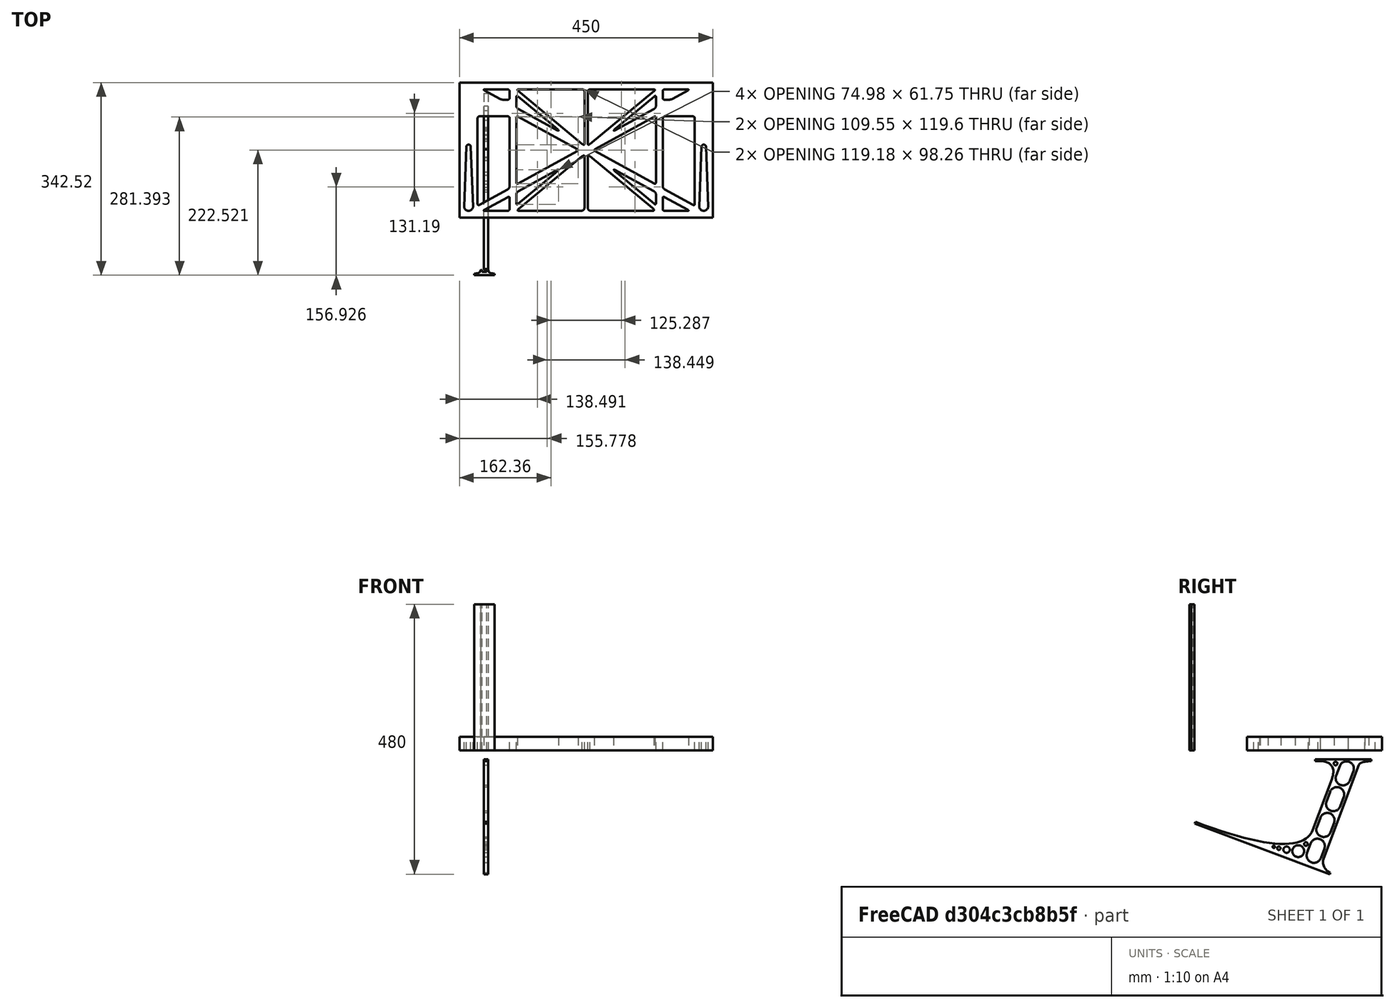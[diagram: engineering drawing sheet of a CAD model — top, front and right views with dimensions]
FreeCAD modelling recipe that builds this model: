
FCSTD DOCUMENT  (FreeCAD 0.19R0.19.2)
Label: laptopStand162FCStd
License: All rights reserved
LicenseURL: http://en.wikipedia.org/wiki/All_rights_reserved
objects: Sketcher::SketchObject×4, Part::Extrusion×3
note: 7 computed .brp shape members not serialized (recipe doc carries the construction recipe); baked Part::Feature solids carry a one-line shape summary decoded from their .brp

FEATURE [Sketcher::SketchObject] Sketch
  FullyConstrained = false
  sketch-geometry (349):
    g0: LineSegment StartX=-10.9272 StartY=-82.7794 StartZ=0 EndX=46.0728 EndY=-51.4823 EndZ=0
    g1: LineSegment StartX=-10.9272 StartY=76.4095 StartZ=0 EndX=-10.9272 EndY=-82.7794 EndZ=0
    g2: LineSegment StartX=46.0728 StartY=76.4095 StartZ=0 EndX=46.0728 EndY=-51.4823 EndZ=0
    g3: LineSegment StartX=-42.9272 StartY=136.221 StartZ=0 EndX=-42.9272 EndY=-103.779 EndZ=0
    g4: LineSegment StartX=407.073 StartY=136.221 StartZ=0 EndX=407.073 EndY=-103.779 EndZ=0
    g5: ArcOfCircle CenterX=-26.9272 CenterY=-83.7794 CenterZ=0 NormalX=0 NormalY=0 NormalZ=1 AngleXU=0 Radius=8 StartAngle=3.14159 EndAngle=6.28319
    g6: ArcOfCircle CenterX=391.073 CenterY=22.1087 CenterZ=0 NormalX=0 NormalY=0 NormalZ=1 AngleXU=0 Radius=8 StartAngle=-4.4e-15 EndAngle=3.14159
    g7: LineSegment StartX=399.073 StartY=22.1087 StartZ=0 EndX=399.073 EndY=-83.7794 EndZ=0
    g8: LineSegment StartX=383.073 StartY=22.1087 StartZ=0 EndX=383.073 EndY=-83.7794 EndZ=0
    g9: ArcOfCircle CenterX=391.073 CenterY=-83.7794 CenterZ=0 NormalX=0 NormalY=0 NormalZ=1 AngleXU=0 Radius=8 StartAngle=3.14159 EndAngle=6.28319
    g10: Circle CenterX=175.022 CenterY=27.0628 CenterZ=0 NormalX=0 NormalY=0 NormalZ=1 AngleXU=0 Radius=1
    g11: Circle CenterX=179.022 CenterY=24.8665 CenterZ=0 NormalX=0 NormalY=0 NormalZ=1 AngleXU=0 Radius=1
    g12: Circle CenterX=179.022 CenterY=27.0628 CenterZ=0 NormalX=0 NormalY=0 NormalZ=1 AngleXU=0 Radius=1
    g13: BSplineCurve PolesCount=3 KnotsCount=2 Degree=2 IsPeriodic=0
    g14: GeomPoint X=175.022 Y=27.0628 Z=0
    g15: GeomPoint X=179.022 Y=27.0628 Z=0
    g16: Circle CenterX=189.124 CenterY=27.0628 CenterZ=0 NormalX=0 NormalY=0 NormalZ=1 AngleXU=0 Radius=1
    g17: Circle CenterX=185.124 CenterY=24.8665 CenterZ=0 NormalX=0 NormalY=0 NormalZ=1 AngleXU=0 Radius=1
    g18: Circle CenterX=185.124 CenterY=27.0628 CenterZ=0 NormalX=0 NormalY=0 NormalZ=1 AngleXU=0 Radius=1
    g19: BSplineCurve PolesCount=3 KnotsCount=2 Degree=2 IsPeriodic=0
    g20: GeomPoint X=189.124 Y=27.0628 Z=0
    g21: GeomPoint X=185.124 Y=27.0628 Z=0
    g22: Circle CenterX=175.022 CenterY=5.37834 CenterZ=0 NormalX=0 NormalY=0 NormalZ=1 AngleXU=0 Radius=1
    g23: Circle CenterX=179.022 CenterY=7.57463 CenterZ=0 NormalX=0 NormalY=0 NormalZ=1 AngleXU=0 Radius=1
    g24: Circle CenterX=179.022 CenterY=5.34704 CenterZ=0 NormalX=0 NormalY=0 NormalZ=1 AngleXU=0 Radius=1
    g25: BSplineCurve PolesCount=3 KnotsCount=2 Degree=2 IsPeriodic=0
    g26: GeomPoint X=175.022 Y=5.37834 Z=0
    g27: GeomPoint X=179.022 Y=5.34704 Z=0
    g28: Circle CenterX=189.124 CenterY=5.37834 CenterZ=0 NormalX=0 NormalY=0 NormalZ=1 AngleXU=0 Radius=1
    g29: Circle CenterX=185.124 CenterY=7.57463 CenterZ=0 NormalX=0 NormalY=0 NormalZ=1 AngleXU=0 Radius=1
    g30: Circle CenterX=185.124 CenterY=5.34704 CenterZ=0 NormalX=0 NormalY=0 NormalZ=1 AngleXU=0 Radius=1
    g31: BSplineCurve PolesCount=3 KnotsCount=2 Degree=2 IsPeriodic=0
    g32: GeomPoint X=189.124 Y=5.37834 Z=0
    g33: GeomPoint X=185.124 Y=5.34704 Z=0
    g34: Circle CenterX=165.871 CenterY=18.1458 CenterZ=0 NormalX=0 NormalY=0 NormalZ=1 AngleXU=0 Radius=1
    g35: Circle CenterX=169.377 CenterY=16.2206 CenterZ=0 NormalX=0 NormalY=0 NormalZ=1 AngleXU=0 Radius=1
    g36: Circle CenterX=165.871 CenterY=14.2954 CenterZ=0 NormalX=0 NormalY=0 NormalZ=1 AngleXU=0 Radius=1
    g37: BSplineCurve PolesCount=3 KnotsCount=2 Degree=2 IsPeriodic=0
    g38: GeomPoint X=165.871 Y=18.1458 Z=0
    g39: GeomPoint X=165.871 Y=14.2954 Z=0
    g40: Circle CenterX=198.275 CenterY=18.1458 CenterZ=0 NormalX=0 NormalY=0 NormalZ=1 AngleXU=0 Radius=1
    g41: Circle CenterX=194.768 CenterY=16.2206 CenterZ=0 NormalX=0 NormalY=0 NormalZ=1 AngleXU=0 Radius=1
    g42: Circle CenterX=198.275 CenterY=14.2954 CenterZ=0 NormalX=0 NormalY=0 NormalZ=1 AngleXU=0 Radius=1
    g43: BSplineCurve PolesCount=3 KnotsCount=2 Degree=2 IsPeriodic=0
    g44: GeomPoint X=198.275 Y=18.1458 Z=0
    g45: GeomPoint X=198.275 Y=14.2954 Z=0
    g46: LineSegment StartX=407.073 StartY=-103.779 StartZ=0 EndX=-42.9272 EndY=-103.779 EndZ=0
    g47: LineSegment StartX=407.073 StartY=136.221 StartZ=0 EndX=-42.9272 EndY=136.221 EndZ=0
    g48: LineSegment StartX=46.0728 StartY=76.4095 StartZ=0 EndX=-10.9272 EndY=76.4095 EndZ=0
    g49: Circle CenterX=125.607 CenterY=54.1951 CenterZ=0 NormalX=0 NormalY=0 NormalZ=1 AngleXU=0 Radius=1
    g50: Circle CenterX=139.632 CenterY=46.4944 CenterZ=0 NormalX=0 NormalY=0 NormalZ=1 AngleXU=0 Radius=1
    g51: Circle CenterX=127.326 CenterY=56.7187 CenterZ=0 NormalX=0 NormalY=0 NormalZ=1 AngleXU=0 Radius=1
    g52: BSplineCurve PolesCount=3 KnotsCount=2 Degree=2 IsPeriodic=0
    g53: GeomPoint X=125.607 Y=54.1951 Z=0
    g54: GeomPoint X=127.326 Y=56.7187 Z=0
    g55: Circle CenterX=236.821 CenterY=56.7187 CenterZ=0 NormalX=0 NormalY=0 NormalZ=1 AngleXU=0 Radius=1
    g56: Circle CenterX=224.513 CenterY=46.4944 CenterZ=0 NormalX=0 NormalY=0 NormalZ=1 AngleXU=0 Radius=1
    g57: Circle CenterX=238.538 CenterY=54.1951 CenterZ=0 NormalX=0 NormalY=0 NormalZ=1 AngleXU=0 Radius=1
    g58: BSplineCurve PolesCount=3 KnotsCount=2 Degree=2 IsPeriodic=0
    g59: GeomPoint X=236.821 Y=56.7187 Z=0
    g60: GeomPoint X=238.538 Y=54.1951 Z=0
    g61: Circle CenterX=238.538 CenterY=-21.7539 CenterZ=0 NormalX=0 NormalY=0 NormalZ=1 AngleXU=0 Radius=1
    g62: Circle CenterX=224.513 CenterY=-14.0532 CenterZ=0 NormalX=0 NormalY=0 NormalZ=1 AngleXU=0 Radius=1
    g63: Circle CenterX=236.821 CenterY=-24.2775 CenterZ=0 NormalX=0 NormalY=0 NormalZ=1 AngleXU=0 Radius=1
    g64: BSplineCurve PolesCount=3 KnotsCount=2 Degree=2 IsPeriodic=0
    g65: GeomPoint X=238.538 Y=-21.7539 Z=0
    g66: GeomPoint X=236.821 Y=-24.2775 Z=0
    g67: Circle CenterX=125.607 CenterY=-21.7539 CenterZ=0 NormalX=0 NormalY=0 NormalZ=1 AngleXU=0 Radius=1
    g68: Circle CenterX=139.632 CenterY=-14.0532 CenterZ=0 NormalX=0 NormalY=0 NormalZ=1 AngleXU=0 Radius=1
    g69: Circle CenterX=127.325 CenterY=-24.2775 CenterZ=0 NormalX=0 NormalY=0 NormalZ=1 AngleXU=0 Radius=1
    g70: BSplineCurve PolesCount=3 KnotsCount=2 Degree=2 IsPeriodic=0
    g71: GeomPoint X=125.607 Y=-21.7539 Z=0
    g72: GeomPoint X=127.325 Y=-24.2775 Z=0
    g73: Circle CenterX=302.996 CenterY=111.695 CenterZ=0 NormalX=0 NormalY=0 NormalZ=1 AngleXU=0 Radius=1
    g74: Circle CenterX=306.073 CenterY=114.251 CenterZ=0 NormalX=0 NormalY=0 NormalZ=1 AngleXU=0 Radius=1
    g75: Circle CenterX=306.073 CenterY=110.251 CenterZ=0 NormalX=0 NormalY=0 NormalZ=1 AngleXU=0 Radius=1
    g76: BSplineCurve PolesCount=3 KnotsCount=2 Degree=2 IsPeriodic=0
    g77: GeomPoint X=302.996 Y=111.695 Z=0
    g78: GeomPoint X=306.073 Y=110.251 Z=0
    g79: Circle CenterX=306.073 CenterY=95.2763 CenterZ=0 NormalX=0 NormalY=0 NormalZ=1 AngleXU=0 Radius=1
    g80: Circle CenterX=306.073 CenterY=91.2763 CenterZ=0 NormalX=0 NormalY=0 NormalZ=1 AngleXU=0 Radius=1
    g81: Circle CenterX=302.567 CenterY=89.3511 CenterZ=0 NormalX=0 NormalY=0 NormalZ=1 AngleXU=0 Radius=1
    g82: BSplineCurve PolesCount=3 KnotsCount=2 Degree=2 IsPeriodic=0
    g83: GeomPoint X=306.073 Y=95.2763 Z=0
    g84: GeomPoint X=302.567 Y=89.3511 Z=0
    g85: LineSegment StartX=306.073 StartY=110.251 StartZ=0 EndX=306.073 EndY=95.2763 EndZ=0
    g86: LineSegment StartX=302.996 StartY=111.695 StartZ=0 EndX=236.821 EndY=56.7187 EndZ=0
    g87: LineSegment StartX=238.538 StartY=54.1951 StartZ=0 EndX=302.567 EndY=89.3511 EndZ=0
    g88: Circle CenterX=61.1496 CenterY=111.695 CenterZ=0 NormalX=0 NormalY=0 NormalZ=1 AngleXU=0 Radius=1
    g89: Circle CenterX=58.0728 CenterY=114.251 CenterZ=0 NormalX=0 NormalY=0 NormalZ=1 AngleXU=0 Radius=1
    g90: Circle CenterX=58.0728 CenterY=110.251 CenterZ=0 NormalX=0 NormalY=0 NormalZ=1 AngleXU=0 Radius=1
    g91: BSplineCurve PolesCount=3 KnotsCount=2 Degree=2 IsPeriodic=0
    g92: GeomPoint X=61.1496 Y=111.695 Z=0
    g93: GeomPoint X=58.0728 Y=110.251 Z=0
    g94: Circle CenterX=61.5791 CenterY=89.3511 CenterZ=0 NormalX=0 NormalY=0 NormalZ=1 AngleXU=0 Radius=1
    g95: Circle CenterX=58.0728 CenterY=91.2763 CenterZ=0 NormalX=0 NormalY=0 NormalZ=1 AngleXU=0 Radius=1
    g96: Circle CenterX=58.0728 CenterY=95.2763 CenterZ=0 NormalX=0 NormalY=0 NormalZ=1 AngleXU=0 Radius=1
    g97: BSplineCurve PolesCount=3 KnotsCount=2 Degree=2 IsPeriodic=0
    g98: GeomPoint X=61.5791 Y=89.3511 Z=0
    g99: GeomPoint X=58.0728 Y=95.2763 Z=0
    g100: LineSegment StartX=58.0728 StartY=110.251 StartZ=0 EndX=58.0728 EndY=95.2763 EndZ=0
    g101: LineSegment StartX=61.1496 StartY=111.695 StartZ=0 EndX=127.326 EndY=56.7187 EndZ=0
    g102: LineSegment StartX=125.607 StartY=54.1951 StartZ=0 EndX=61.5791 EndY=89.3511 EndZ=0
    g103: Circle CenterX=61.5791 CenterY=-56.9099 CenterZ=0 NormalX=0 NormalY=0 NormalZ=1 AngleXU=0 Radius=1
    g104: Circle CenterX=58.0728 CenterY=-58.8351 CenterZ=0 NormalX=0 NormalY=0 NormalZ=1 AngleXU=0 Radius=1
    g105: Circle CenterX=58.0728 CenterY=-62.8351 CenterZ=0 NormalX=0 NormalY=0 NormalZ=1 AngleXU=0 Radius=1
    g106: BSplineCurve PolesCount=3 KnotsCount=2 Degree=2 IsPeriodic=0
    g107: GeomPoint X=61.5791 Y=-56.9099 Z=0
    g108: GeomPoint X=58.0728 Y=-62.8351 Z=0
    g109: Circle CenterX=58.0728 CenterY=-77.8102 CenterZ=0 NormalX=0 NormalY=0 NormalZ=1 AngleXU=0 Radius=1
    g110: Circle CenterX=58.0728 CenterY=-81.8102 CenterZ=0 NormalX=0 NormalY=0 NormalZ=1 AngleXU=0 Radius=1
    g111: Circle CenterX=61.1496 CenterY=-79.2541 CenterZ=0 NormalX=0 NormalY=0 NormalZ=1 AngleXU=0 Radius=1
    g112: BSplineCurve PolesCount=3 KnotsCount=2 Degree=2 IsPeriodic=0
    g113: GeomPoint X=58.0728 Y=-77.8102 Z=0
    g114: GeomPoint X=61.1496 Y=-79.2541 Z=0
    g115: LineSegment StartX=58.0728 StartY=-62.8351 StartZ=0 EndX=58.0728 EndY=-77.8102 EndZ=0
    g116: LineSegment StartX=61.1496 StartY=-79.2541 StartZ=0 EndX=127.325 EndY=-24.2775 EndZ=0
    g117: LineSegment StartX=125.607 StartY=-21.7539 StartZ=0 EndX=61.5791 EndY=-56.9099 EndZ=0
    g118: Circle CenterX=302.567 CenterY=-56.9099 CenterZ=0 NormalX=0 NormalY=0 NormalZ=1 AngleXU=0 Radius=1
    g119: Circle CenterX=306.073 CenterY=-58.8351 CenterZ=0 NormalX=0 NormalY=0 NormalZ=1 AngleXU=0 Radius=1
    g120: Circle CenterX=306.073 CenterY=-62.8351 CenterZ=0 NormalX=0 NormalY=0 NormalZ=1 AngleXU=0 Radius=1
    g121: BSplineCurve PolesCount=3 KnotsCount=2 Degree=2 IsPeriodic=0
    g122: GeomPoint X=302.567 Y=-56.9099 Z=0
    g123: GeomPoint X=306.073 Y=-62.8351 Z=0
    g124: Circle CenterX=302.996 CenterY=-79.2541 CenterZ=0 NormalX=0 NormalY=0 NormalZ=1 AngleXU=0 Radius=1
    g125: Circle CenterX=306.073 CenterY=-81.8102 CenterZ=0 NormalX=0 NormalY=0 NormalZ=1 AngleXU=0 Radius=1
    g126: Circle CenterX=306.073 CenterY=-77.8102 CenterZ=0 NormalX=0 NormalY=0 NormalZ=1 AngleXU=0 Radius=1
    g127: BSplineCurve PolesCount=3 KnotsCount=2 Degree=2 IsPeriodic=0
    g128: GeomPoint X=302.996 Y=-79.2541 Z=0
    g129: GeomPoint X=306.073 Y=-77.8102 Z=0
    g130: LineSegment StartX=306.073 StartY=-62.8351 StartZ=0 EndX=306.073 EndY=-77.8102 EndZ=0
    g131: LineSegment StartX=302.996 StartY=-79.2541 StartZ=0 EndX=236.821 EndY=-24.2775 EndZ=0
    g132: LineSegment StartX=238.538 StartY=-21.7539 StartZ=0 EndX=302.567 EndY=-56.9099 EndZ=0
    g133: Circle CenterX=61.6457 CenterY=-88.8112 CenterZ=0 NormalX=0 NormalY=0 NormalZ=1 AngleXU=0 Radius=1
    g134: Circle CenterX=58.0728 CenterY=-91.7794 CenterZ=0 NormalX=0 NormalY=0 NormalZ=1 AngleXU=0 Radius=1
    g135: Circle CenterX=63.9135 CenterY=-91.7794 CenterZ=0 NormalX=0 NormalY=0 NormalZ=1 AngleXU=0 Radius=1
    g136: BSplineCurve PolesCount=3 KnotsCount=2 Degree=2 IsPeriodic=0
    g137: GeomPoint X=61.6457 Y=-88.8112 Z=0
    g138: GeomPoint X=63.9135 Y=-91.7794 Z=0
    g139: Circle CenterX=179.022 CenterY=-85.8163 CenterZ=0 NormalX=0 NormalY=0 NormalZ=1 AngleXU=0 Radius=1
    g140: Circle CenterX=179.022 CenterY=-91.7794 CenterZ=0 NormalX=0 NormalY=0 NormalZ=1 AngleXU=0 Radius=1
    g141: Circle CenterX=171.895 CenterY=-91.7794 CenterZ=0 NormalX=0 NormalY=0 NormalZ=1 AngleXU=0 Radius=1
    g142: BSplineCurve PolesCount=3 KnotsCount=2 Degree=2 IsPeriodic=0
    g143: GeomPoint X=179.022 Y=-85.8163 Z=0
    g144: GeomPoint X=171.895 Y=-91.7794 Z=0
    g145: Circle CenterX=185.124 CenterY=-86.2028 CenterZ=0 NormalX=0 NormalY=0 NormalZ=1 AngleXU=0 Radius=1
    g146: Circle CenterX=185.124 CenterY=-91.7794 CenterZ=0 NormalX=0 NormalY=0 NormalZ=1 AngleXU=0 Radius=1
    g147: Circle CenterX=191.747 CenterY=-91.7794 CenterZ=0 NormalX=0 NormalY=0 NormalZ=1 AngleXU=0 Radius=1
    g148: BSplineCurve PolesCount=3 KnotsCount=2 Degree=2 IsPeriodic=0
    g149: GeomPoint X=185.124 Y=-86.2028 Z=0
    g150: GeomPoint X=191.747 Y=-91.7794 Z=0
    g151: Circle CenterX=299.888 CenterY=-86.6413 CenterZ=0 NormalX=0 NormalY=0 NormalZ=1 AngleXU=0 Radius=1
    g152: Circle CenterX=306.073 CenterY=-91.7794 CenterZ=0 NormalX=0 NormalY=0 NormalZ=1 AngleXU=0 Radius=1
    g153: Circle CenterX=298.776 CenterY=-91.7794 CenterZ=0 NormalX=0 NormalY=0 NormalZ=1 AngleXU=0 Radius=1
    g154: BSplineCurve PolesCount=3 KnotsCount=2 Degree=2 IsPeriodic=0
    g155: GeomPoint X=299.888 Y=-86.6413 Z=0
    g156: GeomPoint X=298.776 Y=-91.7794 Z=0
    g157: LineSegment StartX=189.124 StartY=5.37834 StartZ=0 EndX=299.888 EndY=-86.6413 EndZ=0
    g158: LineSegment StartX=298.776 StartY=-91.7794 StartZ=0 EndX=191.747 EndY=-91.7794 EndZ=0
    g159: LineSegment StartX=185.124 StartY=-86.2028 StartZ=0 EndX=185.124 EndY=5.34704 EndZ=0
    g160: LineSegment StartX=179.022 StartY=5.34704 StartZ=0 EndX=179.022 EndY=-85.8163 EndZ=0
    g161: LineSegment StartX=171.895 StartY=-91.7794 StartZ=0 EndX=63.9135 EndY=-91.7794 EndZ=0
    g162: LineSegment StartX=61.6457 StartY=-88.8112 StartZ=0 EndX=175.022 EndY=5.37834 EndZ=0
    g163: Circle CenterX=302.073 CenterY=124.221 CenterZ=0 NormalX=0 NormalY=0 NormalZ=1 AngleXU=0 Radius=1
    g164: Circle CenterX=306.073 CenterY=124.221 CenterZ=0 NormalX=0 NormalY=0 NormalZ=1 AngleXU=0 Radius=1
    g165: Circle CenterX=302.996 CenterY=121.665 CenterZ=0 NormalX=0 NormalY=0 NormalZ=1 AngleXU=0 Radius=1
    g166: BSplineCurve PolesCount=3 KnotsCount=2 Degree=2 IsPeriodic=0
    g167: GeomPoint X=302.073 Y=124.221 Z=0
    g168: GeomPoint X=302.996 Y=121.665 Z=0
    g169: Circle CenterX=189.124 CenterY=124.221 CenterZ=0 NormalX=0 NormalY=0 NormalZ=1 AngleXU=0 Radius=1
    g170: Circle CenterX=185.124 CenterY=124.221 CenterZ=0 NormalX=0 NormalY=0 NormalZ=1 AngleXU=0 Radius=1
    g171: Circle CenterX=185.124 CenterY=120.221 CenterZ=0 NormalX=0 NormalY=0 NormalZ=1 AngleXU=0 Radius=1
    g172: BSplineCurve PolesCount=3 KnotsCount=2 Degree=2 IsPeriodic=0
    g173: GeomPoint X=189.124 Y=124.221 Z=0
    g174: GeomPoint X=185.124 Y=120.221 Z=0
    g175: Circle CenterX=175.022 CenterY=124.221 CenterZ=0 NormalX=0 NormalY=0 NormalZ=1 AngleXU=0 Radius=1
    g176: Circle CenterX=179.022 CenterY=124.221 CenterZ=0 NormalX=0 NormalY=0 NormalZ=1 AngleXU=0 Radius=1
    g177: Circle CenterX=179.022 CenterY=120.221 CenterZ=0 NormalX=0 NormalY=0 NormalZ=1 AngleXU=0 Radius=1
    g178: BSplineCurve PolesCount=3 KnotsCount=2 Degree=2 IsPeriodic=0
    g179: GeomPoint X=175.022 Y=124.221 Z=0
    g180: GeomPoint X=179.022 Y=120.221 Z=0
    g181: Circle CenterX=62.0728 CenterY=124.221 CenterZ=0 NormalX=0 NormalY=0 NormalZ=1 AngleXU=0 Radius=1
    g182: Circle CenterX=58.0728 CenterY=124.221 CenterZ=0 NormalX=0 NormalY=0 NormalZ=1 AngleXU=0 Radius=1
    g183: Circle CenterX=61.1496 CenterY=121.665 CenterZ=0 NormalX=0 NormalY=0 NormalZ=1 AngleXU=0 Radius=1
    g184: BSplineCurve PolesCount=3 KnotsCount=2 Degree=2 IsPeriodic=0
    g185: GeomPoint X=62.0728 Y=124.221 Z=0
    g186: GeomPoint X=61.1496 Y=121.665 Z=0
    g187: LineSegment StartX=62.0728 StartY=124.221 StartZ=0 EndX=175.022 EndY=124.221 EndZ=0
    g188: LineSegment StartX=179.022 StartY=120.221 StartZ=0 EndX=179.022 EndY=27.0628 EndZ=0
    g189: LineSegment StartX=185.124 StartY=27.0628 StartZ=0 EndX=185.124 EndY=120.221 EndZ=0
    g190: LineSegment StartX=189.124 StartY=124.221 StartZ=0 EndX=302.073 EndY=124.221 EndZ=0
    g191: LineSegment StartX=302.996 StartY=121.665 StartZ=0 EndX=189.124 EndY=27.0628 EndZ=0
    g192: LineSegment StartX=175.022 StartY=27.0628 StartZ=0 EndX=61.1496 EndY=121.665 EndZ=0
    g193: Circle CenterX=61.5791 CenterY=75.4095 CenterZ=0 NormalX=0 NormalY=0 NormalZ=1 AngleXU=0 Radius=1
    g194: Circle CenterX=58.0728 CenterY=77.3346 CenterZ=0 NormalX=0 NormalY=0 NormalZ=1 AngleXU=0 Radius=1
    g195: Circle CenterX=58.0728 CenterY=73.3346 CenterZ=0 NormalX=0 NormalY=0 NormalZ=1 AngleXU=0 Radius=1
    g196: BSplineCurve PolesCount=3 KnotsCount=2 Degree=2 IsPeriodic=0
    g197: GeomPoint X=61.5791 Y=75.4095 Z=0
    g198: GeomPoint X=58.0728 Y=73.3346 Z=0
    g199: Circle CenterX=58.0728 CenterY=-40.8935 CenterZ=0 NormalX=0 NormalY=0 NormalZ=1 AngleXU=0 Radius=1
    g200: Circle CenterX=58.0728 CenterY=-44.8935 CenterZ=0 NormalX=0 NormalY=0 NormalZ=1 AngleXU=0 Radius=1
    g201: Circle CenterX=61.5791 CenterY=-42.9683 CenterZ=0 NormalX=0 NormalY=0 NormalZ=1 AngleXU=0 Radius=1
    g202: BSplineCurve PolesCount=3 KnotsCount=2 Degree=2 IsPeriodic=0
    g203: GeomPoint X=58.0728 Y=-40.8935 Z=0
    g204: GeomPoint X=61.5791 Y=-42.9683 Z=0
    g205: LineSegment StartX=61.5791 StartY=-42.9683 StartZ=0 EndX=165.871 EndY=14.2954 EndZ=0
    g206: LineSegment StartX=165.871 StartY=18.1458 StartZ=0 EndX=61.5791 EndY=75.4095 EndZ=0
    g207: LineSegment StartX=58.0728 StartY=73.3346 StartZ=0 EndX=58.0728 EndY=-40.8935 EndZ=0
    g208: Circle CenterX=302.567 CenterY=-42.9683 CenterZ=0 NormalX=0 NormalY=0 NormalZ=1 AngleXU=0 Radius=1
    g209: Circle CenterX=306.073 CenterY=-44.8935 CenterZ=0 NormalX=0 NormalY=0 NormalZ=1 AngleXU=0 Radius=1
    g210: Circle CenterX=306.073 CenterY=-40.8935 CenterZ=0 NormalX=0 NormalY=0 NormalZ=1 AngleXU=0 Radius=1
    g211: BSplineCurve PolesCount=3 KnotsCount=2 Degree=2 IsPeriodic=0
    g212: GeomPoint X=302.567 Y=-42.9683 Z=0
    g213: GeomPoint X=306.073 Y=-40.8935 Z=0
    g214: Circle CenterX=306.073 CenterY=73.3346 CenterZ=0 NormalX=0 NormalY=0 NormalZ=1 AngleXU=0 Radius=1
    g215: Circle CenterX=306.073 CenterY=77.3346 CenterZ=0 NormalX=0 NormalY=0 NormalZ=1 AngleXU=0 Radius=1
    g216: Circle CenterX=302.567 CenterY=75.4095 CenterZ=0 NormalX=0 NormalY=0 NormalZ=1 AngleXU=0 Radius=1
    g217: BSplineCurve PolesCount=3 KnotsCount=2 Degree=2 IsPeriodic=0
    g218: GeomPoint X=306.073 Y=73.3346 Z=0
    g219: GeomPoint X=302.567 Y=75.4095 Z=0
    g220: LineSegment StartX=302.567 StartY=-42.9683 StartZ=0 EndX=198.275 EndY=14.2954 EndZ=0
    g221: LineSegment StartX=198.275 StartY=18.1458 StartZ=0 EndX=302.567 EndY=75.4095 EndZ=0
    g222: LineSegment StartX=306.073 StartY=73.3346 StartZ=0 EndX=306.073 EndY=-40.8935 EndZ=0
    g223: LineSegment StartX=322.073 StartY=105.865 StartZ=0 EndX=328.643 EndY=105.865 EndZ=0
    g224: LineSegment StartX=318.073 StartY=120.221 StartZ=0 EndX=318.073 EndY=109.865 EndZ=0
    g225: LineSegment StartX=336.157 StartY=107.779 StartZ=0 EndX=362.567 EndY=122.294 EndZ=0
    g226: Circle CenterX=362.073 CenterY=124.221 CenterZ=0 NormalX=0 NormalY=0 NormalZ=1 AngleXU=0 Radius=1
    g227: Circle CenterX=366.073 CenterY=124.221 CenterZ=0 NormalX=0 NormalY=0 NormalZ=1 AngleXU=0 Radius=1
    g228: Circle CenterX=362.567 CenterY=122.294 CenterZ=0 NormalX=0 NormalY=0 NormalZ=1 AngleXU=0 Radius=1
    g229: BSplineCurve PolesCount=3 KnotsCount=2 Degree=2 IsPeriodic=0
    g230: GeomPoint X=362.073 Y=124.221 Z=0
    g231: GeomPoint X=362.567 Y=122.294 Z=0
    g232: Circle CenterX=322.073 CenterY=124.221 CenterZ=0 NormalX=0 NormalY=0 NormalZ=1 AngleXU=0 Radius=1
    g233: Circle CenterX=318.073 CenterY=124.221 CenterZ=0 NormalX=0 NormalY=0 NormalZ=1 AngleXU=0 Radius=1
    g234: Circle CenterX=318.073 CenterY=120.221 CenterZ=0 NormalX=0 NormalY=0 NormalZ=1 AngleXU=0 Radius=1
    g235: BSplineCurve PolesCount=3 KnotsCount=2 Degree=2 IsPeriodic=0
    g236: GeomPoint X=322.073 Y=124.221 Z=0
    g237: GeomPoint X=318.073 Y=120.221 Z=0
    g238: Circle CenterX=322.073 CenterY=105.865 CenterZ=0 NormalX=0 NormalY=0 NormalZ=1 AngleXU=0 Radius=1
    g239: Circle CenterX=318.073 CenterY=105.865 CenterZ=0 NormalX=0 NormalY=0 NormalZ=1 AngleXU=0 Radius=1
    g240: Circle CenterX=318.073 CenterY=109.865 CenterZ=0 NormalX=0 NormalY=0 NormalZ=1 AngleXU=0 Radius=1
    g241: BSplineCurve PolesCount=3 KnotsCount=2 Degree=2 IsPeriodic=0
    g242: GeomPoint X=322.073 Y=105.865 Z=0
    g243: GeomPoint X=318.073 Y=109.865 Z=0
    g244: Circle CenterX=336.157 CenterY=107.779 CenterZ=0 NormalX=0 NormalY=0 NormalZ=1 AngleXU=0 Radius=1
    g245: Circle CenterX=332.651 CenterY=105.853 CenterZ=0 NormalX=0 NormalY=0 NormalZ=1 AngleXU=0 Radius=1
    g246: Circle CenterX=328.643 CenterY=105.865 CenterZ=0 NormalX=0 NormalY=0 NormalZ=1 AngleXU=0 Radius=1
    g247: BSplineCurve PolesCount=3 KnotsCount=2 Degree=2 IsPeriodic=0
    g248: GeomPoint X=336.157 Y=107.779 Z=0
    g249: GeomPoint X=328.643 Y=105.865 Z=0
    g250: LineSegment StartX=322.073 StartY=124.221 StartZ=0 EndX=362.073 EndY=124.221 EndZ=0
    g251: Circle CenterX=371.567 CenterY=-80.8644 CenterZ=0 NormalX=0 NormalY=0 NormalZ=1 AngleXU=0 Radius=1
    g252: Circle CenterX=375.073 CenterY=-82.7896 CenterZ=0 NormalX=0 NormalY=0 NormalZ=1 AngleXU=0 Radius=1
    g253: Circle CenterX=375.073 CenterY=-78.7896 CenterZ=0 NormalX=0 NormalY=0 NormalZ=1 AngleXU=0 Radius=1
    g254: BSplineCurve PolesCount=3 KnotsCount=2 Degree=2 IsPeriodic=0
    g255: GeomPoint X=371.567 Y=-80.8644 Z=0
    g256: GeomPoint X=375.073 Y=-78.7896 Z=0
    g257: Circle CenterX=321.579 CenterY=-53.4075 CenterZ=0 NormalX=0 NormalY=0 NormalZ=1 AngleXU=0 Radius=1
    g258: Circle CenterX=318.073 CenterY=-51.4823 CenterZ=0 NormalX=0 NormalY=0 NormalZ=1 AngleXU=0 Radius=1
    g259: Circle CenterX=318.073 CenterY=-47.4805 CenterZ=0 NormalX=0 NormalY=0 NormalZ=1 AngleXU=0 Radius=1
    g260: BSplineCurve PolesCount=3 KnotsCount=2 Degree=2 IsPeriodic=0
    g261: GeomPoint X=321.579 Y=-53.4075 Z=0
    g262: GeomPoint X=318.073 Y=-47.4805 Z=0
    g263: LineSegment StartX=371.567 StartY=-80.8644 StartZ=0 EndX=321.579 EndY=-53.4075 EndZ=0
    g264: Circle CenterX=321.579 CenterY=-67.3492 CenterZ=0 NormalX=0 NormalY=0 NormalZ=1 AngleXU=0 Radius=1
    g265: Circle CenterX=318.073 CenterY=-65.424 CenterZ=0 NormalX=0 NormalY=0 NormalZ=1 AngleXU=0 Radius=1
    g266: Circle CenterX=318.073 CenterY=-69.424 CenterZ=0 NormalX=0 NormalY=0 NormalZ=1 AngleXU=0 Radius=1
    g267: BSplineCurve PolesCount=3 KnotsCount=2 Degree=2 IsPeriodic=0
    g268: GeomPoint X=321.579 Y=-67.3492 Z=0
    g269: GeomPoint X=318.073 Y=-69.424 Z=0
    g270: Circle CenterX=362.567 CenterY=-89.8542 CenterZ=0 NormalX=0 NormalY=0 NormalZ=1 AngleXU=0 Radius=1
    g271: Circle CenterX=366.073 CenterY=-91.7794 CenterZ=0 NormalX=0 NormalY=0 NormalZ=1 AngleXU=0 Radius=1
    g272: Circle CenterX=362.073 CenterY=-91.7794 CenterZ=0 NormalX=0 NormalY=0 NormalZ=1 AngleXU=0 Radius=1
    g273: BSplineCurve PolesCount=3 KnotsCount=2 Degree=2 IsPeriodic=0
    g274: GeomPoint X=362.567 Y=-89.8542 Z=0
    g275: GeomPoint X=362.073 Y=-91.7794 Z=0
    g276: Circle CenterX=322.073 CenterY=-91.7794 CenterZ=0 NormalX=0 NormalY=0 NormalZ=1 AngleXU=0 Radius=1
    g277: Circle CenterX=318.073 CenterY=-91.7794 CenterZ=0 NormalX=0 NormalY=0 NormalZ=1 AngleXU=0 Radius=1
    g278: Circle CenterX=318.073 CenterY=-87.7794 CenterZ=0 NormalX=0 NormalY=0 NormalZ=1 AngleXU=0 Radius=1
    g279: BSplineCurve PolesCount=3 KnotsCount=2 Degree=2 IsPeriodic=0
    g280: GeomPoint X=322.073 Y=-91.7794 Z=0
    g281: GeomPoint X=318.073 Y=-87.7794 Z=0
    g282: LineSegment StartX=362.567 StartY=-89.8542 StartZ=0 EndX=321.579 EndY=-67.3492 EndZ=0
    g283: LineSegment StartX=318.073 StartY=-69.424 StartZ=0 EndX=318.073 EndY=-87.7794 EndZ=0
    g284: LineSegment StartX=322.073 StartY=-91.7794 StartZ=0 EndX=362.073 EndY=-91.7794 EndZ=0
    g285: Circle CenterX=2.07281 CenterY=124.221 CenterZ=0 NormalX=0 NormalY=0 NormalZ=1 AngleXU=0 Radius=1
    g286: Circle CenterX=1.57905 CenterY=122.295 CenterZ=0 NormalX=0 NormalY=0 NormalZ=1 AngleXU=0 Radius=1
    g287: BSplineCurve PolesCount=3 KnotsCount=2 Degree=2 IsPeriodic=0
    g288: GeomPoint X=2.07281 Y=124.221 Z=0
    g289: GeomPoint X=1.57905 Y=122.295 Z=0
    g290: Circle CenterX=42.0728 CenterY=124.221 CenterZ=0 NormalX=0 NormalY=0 NormalZ=1 AngleXU=0 Radius=1
    g291: Circle CenterX=46.0728 CenterY=124.221 CenterZ=0 NormalX=0 NormalY=0 NormalZ=1 AngleXU=0 Radius=1
    g292: Circle CenterX=46.0728 CenterY=120.221 CenterZ=0 NormalX=0 NormalY=0 NormalZ=1 AngleXU=0 Radius=1
    g293: BSplineCurve PolesCount=3 KnotsCount=2 Degree=2 IsPeriodic=0
    g294: GeomPoint X=42.0728 Y=124.221 Z=0
    g295: GeomPoint X=46.0728 Y=120.221 Z=0
    g296: Circle CenterX=46.0728 CenterY=109.865 CenterZ=0 NormalX=0 NormalY=0 NormalZ=1 AngleXU=0 Radius=1
    g297: Circle CenterX=46.0728 CenterY=105.865 CenterZ=0 NormalX=0 NormalY=0 NormalZ=1 AngleXU=0 Radius=1
    g298: Circle CenterX=42.0728 CenterY=105.865 CenterZ=0 NormalX=0 NormalY=0 NormalZ=1 AngleXU=0 Radius=1
    g299: BSplineCurve PolesCount=3 KnotsCount=2 Degree=2 IsPeriodic=0
    g300: GeomPoint X=46.0728 Y=109.865 Z=0
    g301: GeomPoint X=42.0728 Y=105.865 Z=0
    g302: Circle CenterX=35.5028 CenterY=105.865 CenterZ=0 NormalX=0 NormalY=0 NormalZ=1 AngleXU=0 Radius=1
    g303: Circle CenterX=31.5028 CenterY=105.865 CenterZ=0 NormalX=0 NormalY=0 NormalZ=1 AngleXU=0 Radius=1
    g304: Circle CenterX=27.9965 CenterY=107.79 CenterZ=0 NormalX=0 NormalY=0 NormalZ=1 AngleXU=0 Radius=1
    g305: BSplineCurve PolesCount=3 KnotsCount=2 Degree=2 IsPeriodic=0
    g306: GeomPoint X=35.5028 Y=105.865 Z=0
    g307: GeomPoint X=27.9965 Y=107.79 Z=0
    g308: LineSegment StartX=2.07281 StartY=124.221 StartZ=0 EndX=42.0728 EndY=124.221 EndZ=0
    g309: LineSegment StartX=46.0728 StartY=120.221 StartZ=0 EndX=46.0728 EndY=109.865 EndZ=0
    g310: LineSegment StartX=42.0728 StartY=105.865 StartZ=0 EndX=35.5028 EndY=105.865 EndZ=0
    g311: LineSegment StartX=27.9965 StartY=107.79 StartZ=0 EndX=1.57905 EndY=122.295 EndZ=0
    g312: Circle CenterX=42.5666 CenterY=-67.3492 CenterZ=0 NormalX=0 NormalY=0 NormalZ=1 AngleXU=0 Radius=1
    g313: Circle CenterX=46.0728 CenterY=-65.424 CenterZ=0 NormalX=0 NormalY=0 NormalZ=1 AngleXU=0 Radius=1
    g314: Circle CenterX=46.0728 CenterY=-69.424 CenterZ=0 NormalX=0 NormalY=0 NormalZ=1 AngleXU=0 Radius=1
    g315: BSplineCurve PolesCount=3 KnotsCount=2 Degree=2 IsPeriodic=0
    g316: GeomPoint X=42.5666 Y=-67.3492 Z=0
    g317: GeomPoint X=46.0728 Y=-69.424 Z=0
    g318: Circle CenterX=46.0728 CenterY=-87.7794 CenterZ=0 NormalX=0 NormalY=0 NormalZ=1 AngleXU=0 Radius=1
    g319: Circle CenterX=46.0728 CenterY=-91.7794 CenterZ=0 NormalX=0 NormalY=0 NormalZ=1 AngleXU=0 Radius=1
    g320: Circle CenterX=42.0728 CenterY=-91.7794 CenterZ=0 NormalX=0 NormalY=0 NormalZ=1 AngleXU=0 Radius=1
    g321: BSplineCurve PolesCount=3 KnotsCount=2 Degree=2 IsPeriodic=0
    g322: GeomPoint X=46.0728 Y=-87.7794 Z=0
    g323: GeomPoint X=42.0728 Y=-91.7794 Z=0
    g324: Circle CenterX=2.07281 CenterY=-91.7794 CenterZ=0 NormalX=0 NormalY=0 NormalZ=1 AngleXU=0 Radius=1
    g325: Circle CenterX=-1.92719 CenterY=-91.7794 CenterZ=0 NormalX=0 NormalY=0 NormalZ=1 AngleXU=0 Radius=1
    g326: Circle CenterX=1.57905 CenterY=-89.8542 CenterZ=0 NormalX=0 NormalY=0 NormalZ=1 AngleXU=0 Radius=1
    g327: BSplineCurve PolesCount=3 KnotsCount=2 Degree=2 IsPeriodic=0
    g328: GeomPoint X=2.07281 Y=-91.7794 Z=0
    g329: GeomPoint X=1.57905 Y=-89.8542 Z=0
    g330: LineSegment StartX=2.07281 StartY=-91.7794 StartZ=0 EndX=42.0728 EndY=-91.7794 EndZ=0
    g331: LineSegment StartX=46.0728 StartY=-87.7794 StartZ=0 EndX=46.0728 EndY=-69.424 EndZ=0
    g332: LineSegment StartX=42.5666 StartY=-67.3492 StartZ=0 EndX=1.57905 EndY=-89.8542 EndZ=0
    g333: Circle CenterX=322.073 CenterY=76.4095 CenterZ=0 NormalX=0 NormalY=0 NormalZ=1 AngleXU=0 Radius=4
    g334: BSplineCurve PolesCount=3 KnotsCount=2 Degree=2 IsPeriodic=0
    g335: GeomPoint X=318.073 Y=72.4095 Z=0
    g336: GeomPoint X=322.073 Y=76.4095 Z=0
    g337: Circle CenterX=375.073 CenterY=72.4095 CenterZ=0 NormalX=0 NormalY=0 NormalZ=1 AngleXU=0 Radius=1
    g338: Circle CenterX=375.073 CenterY=76.4095 CenterZ=0 NormalX=0 NormalY=0 NormalZ=1 AngleXU=0 Radius=1
    g339: Circle CenterX=371.073 CenterY=76.4095 CenterZ=0 NormalX=0 NormalY=0 NormalZ=1 AngleXU=0 Radius=1
    g340: BSplineCurve PolesCount=3 KnotsCount=2 Degree=2 IsPeriodic=0
    g341: GeomPoint X=375.073 Y=72.4095 Z=0
    g342: GeomPoint X=371.073 Y=76.4095 Z=0
    g343: LineSegment StartX=322.073 StartY=76.4095 StartZ=0 EndX=371.073 EndY=76.4095 EndZ=0
    g344: LineSegment StartX=318.073 StartY=72.4095 StartZ=0 EndX=318.073 EndY=-47.4805 EndZ=0
    g345: LineSegment StartX=375.073 StartY=72.4095 StartZ=0 EndX=375.073 EndY=-78.7896 EndZ=0
    g346: ArcOfCircle CenterX=-26.9272 CenterY=22.1087 CenterZ=0 NormalX=0 NormalY=0 NormalZ=1 AngleXU=0 Radius=4 StartAngle=5e-16 EndAngle=3.14159
    g347: LineSegment StartX=-30.9272 StartY=22.1087 StartZ=0 EndX=-34.9272 EndY=-83.7794 EndZ=0
    g348: LineSegment StartX=-18.9272 StartY=-83.7794 StartZ=0 EndX=-22.9272 EndY=22.1087 EndZ=0
  constraints (572):
    c: Coincident(g0,g2)
    c: Block(g0)
    c: Block(g1)
    c: Vertical(g3)
    c: Vertical(g4)
    c: Block(g4)
    c: Block(g3)
    c: Tangent(g6,g7) = 1.5708
    c: Tangent(g7,g9) = 1.5708
    c: Equal(g6,g9)
    c: Coincident(g8,g6)
    c: Coincident(g8,g9)
    c: Block(g7)
    c: Block(g8)
    c: Weight(g10) = 1
    c: Equal(g10,g11)
    c: Equal(g10,g12)
    c: InternalAlignment(g10,g13)
    c: InternalAlignment(g11,g13)
    c: InternalAlignment(g12,g13)
    c: InternalAlignment(g14,g13)
    c: InternalAlignment(g15,g13)
    c: Weight(g16) = 1
    c: Equal(g16,g17)
    c: Equal(g16,g18)
    c: InternalAlignment(g16,g19)
    c: InternalAlignment(g17,g19)
    c: InternalAlignment(g18,g19)
    c: InternalAlignment(g20,g19)
    c: InternalAlignment(g21,g19)
    c: Block(g19)
    c: Block(g13)
    c: Weight(g22) = 1
    c: Equal(g22,g23)
    c: Equal(g22,g24)
    c: InternalAlignment(g22,g25)
    c: InternalAlignment(g23,g25)
    c: InternalAlignment(g24,g25)
    c: InternalAlignment(g26,g25)
    c: InternalAlignment(g27,g25)
    c: Weight(g28) = 1
    c: Equal(g28,g29)
    c: Equal(g28,g30)
    c: InternalAlignment(g28,g31)
    c: InternalAlignment(g29,g31)
    c: InternalAlignment(g30,g31)
    c: InternalAlignment(g32,g31)
    c: InternalAlignment(g33,g31)
    c: Block(g31)
    c: Block(g25)
    c: Weight(g34) = 1
    c: Equal(g34,g35)
    c: Equal(g34,g36)
    c: InternalAlignment(g34,g37)
    c: InternalAlignment(g35,g37)
    c: InternalAlignment(g36,g37)
    c: InternalAlignment(g38,g37)
    c: InternalAlignment(g39,g37)
    c: Weight(g40) = 1
    c: Equal(g40,g41)
    c: Equal(g40,g42)
    c: InternalAlignment(g40,g43)
    c: InternalAlignment(g41,g43)
    c: InternalAlignment(g42,g43)
    c: InternalAlignment(g44,g43)
    c: InternalAlignment(g45,g43)
    c: Block(g37)
    c: Block(g43)
    c: Coincident(g46,g4)
    c: Coincident(g46,g3)
    c: Horizontal(g46)
    c: Distance(g46) = 450
    c: Coincident(g47,g4)
    c: Coincident(g47,g3)
    c: Horizontal(g47)
    c: Horizontal(g48)
    c: Coincident(g2,g48)
    c: Block(g48)
    c: Coincident(g1,g48)
    c: Weight(g49) = 1
    c: Equal(g49,g50)
    c: Equal(g49,g51)
    c: InternalAlignment(g49,g52)
    c: InternalAlignment(g50,g52)
    c: InternalAlignment(g51,g52)
    c: InternalAlignment(g53,g52)
    c: InternalAlignment(g54,g52)
    c: Block(g52)
    c: Weight(g55) = 1
    c: Equal(g55,g56)
    c: Equal(g55,g57)
    c: InternalAlignment(g55,g58)
    c: InternalAlignment(g56,g58)
    c: InternalAlignment(g57,g58)
    c: InternalAlignment(g59,g58)
    c: InternalAlignment(g60,g58)
    c: Block(g58)
    c: Weight(g61) = 1
    c: Equal(g61,g62)
    c: Equal(g61,g63)
    c: InternalAlignment(g61,g64)
    c: InternalAlignment(g62,g64)
    c: InternalAlignment(g63,g64)
    c: InternalAlignment(g65,g64)
    c: InternalAlignment(g66,g64)
    c: Block(g64)
    c: Weight(g67) = 1
    c: Equal(g67,g68)
    c: Equal(g67,g69)
    c: InternalAlignment(g67,g70)
    c: InternalAlignment(g68,g70)
    c: InternalAlignment(g69,g70)
    c: InternalAlignment(g71,g70)
    c: InternalAlignment(g72,g70)
    c: Block(g70)
    c: Weight(g73) = 1
    c: Equal(g73,g74)
    c: Equal(g73,g75)
    c: InternalAlignment(g73,g76)
    c: InternalAlignment(g74,g76)
    c: InternalAlignment(g75,g76)
    c: InternalAlignment(g77,g76)
    c: InternalAlignment(g78,g76)
    c: Weight(g79) = 1
    c: Equal(g79,g80)
    c: Equal(g79,g81)
    c: InternalAlignment(g79,g82)
    c: InternalAlignment(g80,g82)
    c: InternalAlignment(g81,g82)
    c: InternalAlignment(g83,g82)
    c: InternalAlignment(g84,g82)
    c: Block(g76)
    c: Block(g82)
    c: Coincident(g85,g76)
    c: Coincident(g85,g82)
    c: Vertical(g85)
    c: Coincident(g86,g76)
    c: Coincident(g86,g58)
    c: Coincident(g87,g58)
    c: Coincident(g87,g82)
    c: Weight(g88) = 1
    c: Equal(g88,g89)
    c: Equal(g88,g90)
    c: InternalAlignment(g88,g91)
    c: InternalAlignment(g89,g91)
    c: InternalAlignment(g90,g91)
    c: InternalAlignment(g92,g91)
    c: InternalAlignment(g93,g91)
    c: Weight(g94) = 1
    c: Equal(g94,g95)
    c: Equal(g94,g96)
    c: InternalAlignment(g94,g97)
    c: InternalAlignment(g95,g97)
    c: InternalAlignment(g96,g97)
    c: InternalAlignment(g98,g97)
    c: InternalAlignment(g99,g97)
    c: Block(g91)
    c: Block(g97)
    c: Coincident(g100,g91)
    c: Coincident(g100,g97)
    c: Vertical(g100)
    c: Coincident(g101,g91)
    c: Coincident(g101,g52)
    c: Coincident(g102,g52)
    c: Coincident(g102,g97)
    c: Weight(g103) = 1
    c: Equal(g103,g104)
    c: Equal(g103,g105)
    c: InternalAlignment(g103,g106)
    c: InternalAlignment(g104,g106)
    c: InternalAlignment(g105,g106)
    c: InternalAlignment(g107,g106)
    c: InternalAlignment(g108,g106)
    c: Weight(g109) = 1
    c: Equal(g109,g110)
    c: Equal(g109,g111)
    c: InternalAlignment(g109,g112)
    c: InternalAlignment(g110,g112)
    c: InternalAlignment(g111,g112)
    c: InternalAlignment(g113,g112)
    c: InternalAlignment(g114,g112)
    c: Block(g106)
    c: Block(g112)
    c: Coincident(g115,g106)
    c: Coincident(g115,g112)
    c: Vertical(g115)
    c: Coincident(g116,g112)
    c: Coincident(g116,g70)
    c: Coincident(g117,g70)
    c: Coincident(g117,g106)
    c: Weight(g118) = 1
    c: Equal(g118,g119)
    c: Equal(g118,g120)
    c: InternalAlignment(g118,g121)
    c: InternalAlignment(g119,g121)
    c: InternalAlignment(g120,g121)
    c: InternalAlignment(g122,g121)
    c: InternalAlignment(g123,g121)
    c: Weight(g124) = 1
    c: Equal(g124,g125)
    c: Equal(g124,g126)
    c: InternalAlignment(g124,g127)
    c: InternalAlignment(g125,g127)
    c: InternalAlignment(g126,g127)
    c: InternalAlignment(g128,g127)
    c: InternalAlignment(g129,g127)
    c: Block(g121)
    c: Block(g127)
    c: Coincident(g130,g121)
    c: Coincident(g130,g127)
    c: Vertical(g130)
    c: Coincident(g131,g127)
    c: Coincident(g131,g64)
    c: Coincident(g132,g64)
    c: Coincident(g132,g121)
    c: Weight(g133) = 1
    c: Equal(g133,g134)
    c: Equal(g133,g135)
    c: InternalAlignment(g133,g136)
    c: InternalAlignment(g134,g136)
    c: InternalAlignment(g135,g136)
    c: InternalAlignment(g137,g136)
    c: InternalAlignment(g138,g136)
    c: Weight(g139) = 1
    c: Equal(g139,g140)
    c: Equal(g139,g141)
    c: InternalAlignment(g139,g142)
    c: InternalAlignment(g140,g142)
    c: InternalAlignment(g141,g142)
    c: InternalAlignment(g143,g142)
    c: InternalAlignment(g144,g142)
    c: Weight(g145) = 1
    c: Equal(g145,g146)
    c: Equal(g145,g147)
    c: InternalAlignment(g145,g148)
    c: InternalAlignment(g146,g148)
    c: InternalAlignment(g147,g148)
    c: InternalAlignment(g149,g148)
    c: InternalAlignment(g150,g148)
    c: Weight(g151) = 1
    c: Equal(g151,g152)
    c: Equal(g151,g153)
    c: InternalAlignment(g151,g154)
    c: InternalAlignment(g152,g154)
    c: InternalAlignment(g153,g154)
    c: InternalAlignment(g155,g154)
    c: InternalAlignment(g156,g154)
    c: Block(g154)
    c: Block(g148)
    c: Block(g142)
    c: Block(g136)
    c: Coincident(g157,g31)
    c: Coincident(g157,g154)
    c: Coincident(g158,g154)
    c: Coincident(g158,g148)
    c: Horizontal(g158)
    c: Coincident(g159,g148)
    c: Coincident(g159,g31)
    c: Vertical(g159)
    c: Coincident(g160,g25)
    c: Coincident(g160,g142)
    c: Vertical(g160)
    c: Coincident(g161,g142)
    c: Coincident(g161,g136)
    c: Horizontal(g161)
    c: Coincident(g162,g136)
    c: Coincident(g162,g25)
    c: Weight(g163) = 1
    c: Equal(g163,g164)
    c: Equal(g163,g165)
    c: InternalAlignment(g163,g166)
    c: InternalAlignment(g164,g166)
    c: InternalAlignment(g165,g166)
    c: InternalAlignment(g167,g166)
    c: InternalAlignment(g168,g166)
    c: Weight(g169) = 1
    c: Equal(g169,g170)
    c: Equal(g169,g171)
    c: InternalAlignment(g169,g172)
    c: InternalAlignment(g170,g172)
    c: InternalAlignment(g171,g172)
    c: InternalAlignment(g173,g172)
    c: InternalAlignment(g174,g172)
    c: Weight(g175) = 1
    c: Equal(g175,g176)
    c: Equal(g175,g177)
    c: InternalAlignment(g175,g178)
    c: InternalAlignment(g176,g178)
    c: InternalAlignment(g177,g178)
    c: InternalAlignment(g179,g178)
    c: InternalAlignment(g180,g178)
    c: Weight(g181) = 1
    c: Equal(g181,g182)
    c: Equal(g181,g183)
    c: InternalAlignment(g181,g184)
    c: InternalAlignment(g182,g184)
    c: InternalAlignment(g183,g184)
    c: InternalAlignment(g185,g184)
    c: InternalAlignment(g186,g184)
    c: Block(g184)
    c: Block(g178)
    c: Block(g172)
    c: Block(g166)
    c: Coincident(g187,g184)
    c: Coincident(g187,g178)
    c: Horizontal(g187)
    c: Coincident(g188,g178)
    c: Coincident(g188,g13)
    c: Vertical(g188)
    c: Coincident(g189,g19)
    c: Coincident(g189,g172)
    c: Vertical(g189)
    c: Coincident(g190,g172)
    c: Coincident(g190,g166)
    c: Horizontal(g190)
    c: Coincident(g191,g166)
    c: Coincident(g191,g19)
    c: Coincident(g192,g13)
    c: Weight(g193) = 1
    c: Equal(g193,g194)
    c: Equal(g193,g195)
    c: InternalAlignment(g193,g196)
    c: InternalAlignment(g194,g196)
    c: InternalAlignment(g195,g196)
    c: InternalAlignment(g197,g196)
    c: InternalAlignment(g198,g196)
    c: Weight(g199) = 1
    c: Equal(g199,g200)
    c: Equal(g199,g201)
    c: InternalAlignment(g199,g202)
    c: InternalAlignment(g200,g202)
    c: InternalAlignment(g201,g202)
    c: InternalAlignment(g203,g202)
    c: InternalAlignment(g204,g202)
    c: Block(g202)
    c: Block(g196)
    c: Coincident(g205,g202)
    c: Coincident(g205,g37)
    c: Coincident(g206,g37)
    c: Coincident(g206,g196)
    c: Coincident(g207,g196)
    c: Coincident(g207,g202)
    c: Vertical(g207)
    c: Weight(g208) = 1
    c: Equal(g208,g209)
    c: Equal(g208,g210)
    c: InternalAlignment(g208,g211)
    c: InternalAlignment(g209,g211)
    c: InternalAlignment(g210,g211)
    c: InternalAlignment(g212,g211)
    c: InternalAlignment(g213,g211)
    c: Weight(g214) = 1
    c: Equal(g214,g215)
    c: Equal(g214,g216)
    c: InternalAlignment(g214,g217)
    c: InternalAlignment(g215,g217)
    c: InternalAlignment(g216,g217)
    c: InternalAlignment(g218,g217)
    c: InternalAlignment(g219,g217)
    c: Block(g217)
    c: Block(g211)
    c: Coincident(g220,g211)
    c: Coincident(g220,g43)
    c: Coincident(g221,g43)
    c: Coincident(g221,g217)
    c: Coincident(g222,g217)
    c: Coincident(g222,g211)
    c: Vertical(g222)
    c: Horizontal(g223)
    c: Block(g223)
    c: Vertical(g224)
    c: Block(g224)
    c: Block(g225)
    c: Weight(g226) = 1
    c: Equal(g226,g227)
    c: Equal(g226,g228)
    c: InternalAlignment(g226,g229)
    c: InternalAlignment(g227,g229)
    c: InternalAlignment(g228,g229)
    c: InternalAlignment(g230,g229)
    c: InternalAlignment(g231,g229)
    c: Weight(g232) = 1
    c: Equal(g232,g233)
    c: Equal(g232,g234)
    c: InternalAlignment(g232,g235)
    c: InternalAlignment(g233,g235)
    c: InternalAlignment(g234,g235)
    c: InternalAlignment(g236,g235)
    c: InternalAlignment(g237,g235)
    c: Weight(g238) = 1
    c: Equal(g238,g239)
    c: Equal(g238,g240)
    c: InternalAlignment(g238,g241)
    c: InternalAlignment(g239,g241)
    c: InternalAlignment(g240,g241)
    c: InternalAlignment(g242,g241)
    c: InternalAlignment(g243,g241)
    c: Weight(g244) = 1
    c: Equal(g244,g245)
    c: Equal(g244,g246)
    c: InternalAlignment(g244,g247)
    c: InternalAlignment(g245,g247)
    c: InternalAlignment(g246,g247)
    c: InternalAlignment(g248,g247)
    c: InternalAlignment(g249,g247)
    c: Block(g229)
    c: Block(g235)
    c: Block(g241)
    c: Block(g247)
    c: Coincident(g250,g235)
    c: Coincident(g250,g229)
    c: Horizontal(g250)
    c: Block(g192)
    c: Weight(g251) = 1
    c: Equal(g251,g252)
    c: Equal(g251,g253)
    c: InternalAlignment(g251,g254)
    c: InternalAlignment(g252,g254)
    c: InternalAlignment(g253,g254)
    c: InternalAlignment(g255,g254)
    c: InternalAlignment(g256,g254)
    c: Weight(g257) = 1
    c: Equal(g257,g258)
    c: Equal(g257,g259)
    c: InternalAlignment(g257,g260)
    c: InternalAlignment(g258,g260)
    c: InternalAlignment(g259,g260)
    c: InternalAlignment(g261,g260)
    c: InternalAlignment(g262,g260)
    c: Block(g254)
    c: Block(g260)
    c: Coincident(g263,g254)
    c: Coincident(g263,g260)
    c: Weight(g264) = 1
    c: Equal(g264,g265)
    c: Equal(g264,g266)
    c: InternalAlignment(g264,g267)
    c: InternalAlignment(g265,g267)
    c: InternalAlignment(g266,g267)
    c: InternalAlignment(g268,g267)
    c: InternalAlignment(g269,g267)
    c: Weight(g270) = 1
    c: Equal(g270,g271)
    c: Equal(g270,g272)
    c: InternalAlignment(g270,g273)
    c: InternalAlignment(g271,g273)
    c: InternalAlignment(g272,g273)
    c: InternalAlignment(g274,g273)
    c: InternalAlignment(g275,g273)
    c: Weight(g276) = 1
    c: Equal(g276,g277)
    c: Equal(g276,g278)
    c: InternalAlignment(g276,g279)
    c: InternalAlignment(g277,g279)
    c: InternalAlignment(g278,g279)
    c: InternalAlignment(g280,g279)
    c: InternalAlignment(g281,g279)
    c: Block(g279)
    c: Block(g273)
    c: Block(g267)
    c: Coincident(g282,g273)
    c: Coincident(g282,g267)
    c: Coincident(g283,g267)
    c: Coincident(g283,g279)
    c: Vertical(g283)
    c: Coincident(g284,g279)
    c: Coincident(g284,g273)
    c: Horizontal(g284)
    c: Weight(g285) = 1
    c: Equal(g285,g286)
    c: InternalAlignment(g285,g287)
    c: InternalAlignment(g286,g287)
    c: InternalAlignment(g288,g287)
    c: InternalAlignment(g289,g287)
    c: Weight(g290) = 1
    c: InternalAlignment(g291,g293)
    c: InternalAlignment(g292,g293)
    c: InternalAlignment(g294,g293)
    c: InternalAlignment(g295,g293)
    c: Weight(g296) = 1
    c: Equal(g296,g297)
    c: Equal(g296,g298)
    c: InternalAlignment(g296,g299)
    c: InternalAlignment(g297,g299)
    c: InternalAlignment(g298,g299)
    c: InternalAlignment(g300,g299)
    c: InternalAlignment(g301,g299)
    c: Equal(g302,g303)
    c: Equal(g302,g304)
    c: InternalAlignment(g302,g305)
    c: InternalAlignment(g303,g305)
    c: InternalAlignment(g304,g305)
    c: InternalAlignment(g306,g305)
    c: InternalAlignment(g307,g305)
    c: Block(g293)
    c: Block(g299)
    c: Block(g305)
    c: Block(g287)
    c: Coincident(g308,g287)
    c: Coincident(g308,g293)
    c: Horizontal(g308)
    c: Coincident(g309,g293)
    c: Coincident(g309,g299)
    c: Vertical(g309)
    c: Coincident(g310,g299)
    c: Coincident(g310,g305)
    c: Horizontal(g310)
    c: Coincident(g311,g305)
    c: Coincident(g311,g287)
    c: Weight(g312) = 1
    c: Equal(g312,g313)
    c: Equal(g312,g314)
    c: InternalAlignment(g312,g315)
    c: InternalAlignment(g313,g315)
    c: InternalAlignment(g314,g315)
    c: InternalAlignment(g316,g315)
    c: InternalAlignment(g317,g315)
    c: Weight(g318) = 1
    c: Equal(g318,g319)
    c: Equal(g318,g320)
    c: InternalAlignment(g318,g321)
    c: InternalAlignment(g319,g321)
    c: InternalAlignment(g320,g321)
    c: InternalAlignment(g322,g321)
    c: InternalAlignment(g323,g321)
    c: Weight(g324) = 1
    c: Equal(g324,g325)
    c: Equal(g324,g326)
    c: InternalAlignment(g324,g327)
    c: InternalAlignment(g325,g327)
    c: InternalAlignment(g326,g327)
    c: InternalAlignment(g328,g327)
    c: InternalAlignment(g329,g327)
    c: Block(g327)
    c: Block(g321)
    c: Block(g315)
    c: Coincident(g330,g327)
    c: Coincident(g330,g321)
    c: Horizontal(g330)
    c: Coincident(g331,g321)
    c: Coincident(g331,g315)
    c: Vertical(g331)
    c: Coincident(g332,g315)
    c: Coincident(g332,g327)
    c: InternalAlignment(g333,g334)
    c: InternalAlignment(g335,g334)
    c: InternalAlignment(g336,g334)
    c: Block(g334)
    c: Equal(g337,g338)
    c: Equal(g337,g339)
    c: InternalAlignment(g337,g340)
    c: InternalAlignment(g338,g340)
    c: InternalAlignment(g339,g340)
    c: InternalAlignment(g341,g340)
    c: InternalAlignment(g342,g340)
    c: Block(g340)
    c: Coincident(g343,g334)
    c: Horizontal(g343)
    c: Block(g343)
    c: Coincident(g344,g334)
    c: Coincident(g344,g260)
    c: Vertical(g344)
    c: Coincident(g345,g340)
    c: Coincident(g345,g254)
    c: Vertical(g345)
    c: Coincident(g347,g5)
    c: Coincident(g348,g5)
    c: Block(g346)
    c: Block(g5)
    c: Block(g348)
    c: Block(g347)
    c: Distance(g344) = 119.89
FEATURE [Sketcher::SketchObject] Sketch001
  FullyConstrained = true
  MapMode = 4
  Placement = pos=(0,0,0) rot=(0.57735,0.57735,0.57735;2.0944rad)
  Support = -> [Sketch]
  sketch-geometry (46):
    g0: BSplineCurve PolesCount=3 KnotsCount=2 Degree=2 IsPeriodic=0
    g1: ArcOfCircle CenterX=73.1223 CenterY=-32.291 CenterZ=0 NormalX=0 NormalY=0 NormalZ=1 AngleXU=0 Radius=13 StartAngle=5.92268 EndAngle=9.06428
    g2: ArcOfCircle CenterX=66.7816 CenterY=-49.1439 CenterZ=0 NormalX=0 NormalY=0 NormalZ=1 AngleXU=0 Radius=13 StartAngle=2.78068 EndAngle=5.92131
    g3: ArcOfCircle CenterX=55.9263 CenterY=-78.1807 CenterZ=0 NormalX=0 NormalY=0 NormalZ=1 AngleXU=0 Radius=13 StartAngle=5.92268 EndAngle=9.06428
    g4: ArcOfCircle CenterX=49.5884 CenterY=-95.0342 CenterZ=0 NormalX=0 NormalY=0 NormalZ=1 AngleXU=0 Radius=13 StartAngle=2.78068 EndAngle=5.92131
    g5: ArcOfCircle CenterX=38.7206 CenterY=-124.067 CenterZ=0 NormalX=0 NormalY=0 NormalZ=1 AngleXU=0 Radius=13 StartAngle=5.92268 EndAngle=9.06428
    g6: ArcOfCircle CenterX=32.3875 CenterY=-140.92 CenterZ=0 NormalX=0 NormalY=0 NormalZ=1 AngleXU=0 Radius=13 StartAngle=2.78068 EndAngle=5.92131
    g7: ArcOfCircle CenterX=21.4715 CenterY=-169.934 CenterZ=0 NormalX=0 NormalY=0 NormalZ=1 AngleXU=0 Radius=13 StartAngle=5.92268 EndAngle=9.06428
    g8: ArcOfCircle CenterX=15.1336 CenterY=-186.787 CenterZ=0 NormalX=0 NormalY=0 NormalZ=1 AngleXU=0 Radius=13 StartAngle=2.78068 EndAngle=5.92131
    g9-g12: Circle x4 (B-spline internal-alignment scaffolding for g13; pole/knot coordinates omitted)
    g13: BSplineCurve PolesCount=4 KnotsCount=2 Degree=3 IsPeriodic=0
    g14: GeomPoint X=28.8094 Y=-19.0875 Z=0
    g15: GeomPoint X=47.0443 Y=-50.4712 Z=0
    g16: Circle CenterX=53.5586 CenterY=-23.2695 CenterZ=0 NormalX=0 NormalY=0 NormalZ=1 AngleXU=0 Radius=3.24518
    g17: Circle CenterX=-195.441 CenterY=-127.082 CenterZ=0 NormalX=0 NormalY=0 NormalZ=1 AngleXU=0 Radius=1
    g18: Circle CenterX=-8.24091 CenterY=-197.481 CenterZ=0 NormalX=0 NormalY=0 NormalZ=1 AngleXU=0 Radius=1
    g19: Circle CenterX=12.8789 CenterY=-141.321 CenterZ=0 NormalX=0 NormalY=0 NormalZ=1 AngleXU=0 Radius=1
    g20: BSplineCurve PolesCount=3 KnotsCount=2 Degree=2 IsPeriodic=0
    g21: GeomPoint X=-195.441 Y=-127.082 Z=0
    g22: GeomPoint X=12.8789 Y=-141.321 Z=0
    g23: Circle CenterX=-12.8016 CenterY=-179.036 CenterZ=0 NormalX=0 NormalY=0 NormalZ=1 AngleXU=0 Radius=10.5072
    g24: Circle CenterX=0.933922 CenterY=-166.43 CenterZ=0 NormalX=0 NormalY=0 NormalZ=1 AngleXU=0 Radius=3.26661
    g25: Circle CenterX=-33.5518 CenterY=-176.44 CenterZ=0 NormalX=0 NormalY=0 NormalZ=1 AngleXU=0 Radius=5.64388
    g26: Circle CenterX=-47.2366 CenterY=-173.859 CenterZ=0 NormalX=0 NormalY=0 NormalZ=1 AngleXU=0 Radius=3.01653
    g27: Circle CenterX=-56.2595 CenterY=-171.456 CenterZ=0 NormalX=0 NormalY=0 NormalZ=1 AngleXU=0 Radius=2.12826
    g28: ArcOfCircle CenterX=51.2151 CenterY=-198.473 CenterZ=0 NormalX=0 NormalY=0 NormalZ=1 AngleXU=0 Radius=20 StartAngle=2.78189 EndAngle=4.35269
    g29: LineSegment StartX=32.4951 StartY=-191.433 StartZ=0 EndX=94.6578 EndY=-26.1352 EndZ=0
    g30: LineSegment StartX=43.1192 StartY=-220.001 StartZ=0 EndX=-196.497 EndY=-129.89 EndZ=0
    g31: LineSegment StartX=43.1192 StartY=-220.001 StartZ=0 EndX=44.1752 EndY=-217.193 EndZ=0
    g32: LineSegment StartX=117.223 StartY=-19.0875 StartZ=0 EndX=117.223 EndY=-16.0875 EndZ=0
    g33: LineSegment StartX=117.223 StartY=-16.0875 StartZ=0 EndX=17.2232 EndY=-16.0875 EndZ=0
    g34: LineSegment StartX=17.2232 StartY=-16.0875 StartZ=0 EndX=17.2232 EndY=-19.0875 EndZ=0
    g35: LineSegment StartX=28.8094 StartY=-19.0875 StartZ=0 EndX=17.2232 EndY=-19.0875 EndZ=0
    g36: LineSegment StartX=47.0443 StartY=-50.4712 StartZ=0 EndX=12.8789 EndY=-141.321 EndZ=0
    g37: LineSegment StartX=-195.441 StartY=-127.082 StartZ=0 EndX=-196.497 EndY=-129.89 EndZ=0
    g38: LineSegment StartX=85.2866 StartY=-36.8766 StartZ=0 EndX=78.9396 EndY=-53.7463 EndZ=0
    g39: LineSegment StartX=60.9579 StartY=-27.7053 StartZ=0 EndX=54.6191 EndY=-44.5532 EndZ=0
    g40: LineSegment StartX=68.0907 StartY=-82.7664 StartZ=0 EndX=61.7465 EndY=-99.6365 EndZ=0
    g41: LineSegment StartX=43.7619 StartY=-73.595 StartZ=0 EndX=37.426 EndY=-90.4435 EndZ=0
    g42: LineSegment StartX=50.885 StartY=-128.652 StartZ=0 EndX=44.5456 EndY=-145.522 EndZ=0
    g43: LineSegment StartX=26.5562 StartY=-119.481 StartZ=0 EndX=20.2251 EndY=-136.329 EndZ=0
    g44: LineSegment StartX=9.3071 StartY=-165.349 StartZ=0 EndX=2.97115 EndY=-182.197 EndZ=0
    g45: LineSegment StartX=33.6358 StartY=-174.52 StartZ=0 EndX=27.2917 EndY=-191.39 EndZ=0
  constraints (71):
    c: Block(g0)
    c: Block(g1)
    c: Block(g2)
    c: Block(g4)
    c: Block(g3)
    c: Block(g6)
    c: Block(g5)
    c: Block(g8)
    c: Block(g7)
    c: Weight(g9) = 1
    c: Equal(g9,g10)
    c: Equal(g9,g11)
    c: Equal(g9,g12)
    c: InternalAlignment(g9-g12 -> g13) x4
    c: InternalAlignment(g14,g13)
    c: InternalAlignment(g15,g13)
    c: Block(g16)
    c: Weight(g17) = 1
    c: Equal(g17,g18)
    c: Equal(g17,g19)
    c: InternalAlignment(g17,g20)
    c: InternalAlignment(g18,g20)
    c: InternalAlignment(g19,g20)
    c: InternalAlignment(g21,g20)
    c: InternalAlignment(g22,g20)
    c: Block(g20)
    c: Block(g23)
    c: Block(g24)
    c: Block(g25)
    c: Block(g26)
    c: Block(g27)
    c: Block(g28)
    c: Coincident(g29,g28)
    c: Coincident(g29,g0)
    c: Block(g13)
    c: Coincident(g31,g30)
    c: Coincident(g31,g28)
    c: Block(g31)
    c: Coincident(g32,g0)
    c: Vertical(g32)
    c: Coincident(g33,g32)
    c: Horizontal(g33)
    c: Coincident(g34,g33)
    c: Vertical(g34)
    c: Block(g33)
    c: Coincident(g35,g13)
    c: Coincident(g35,g34)
    c: Horizontal(g35)
    c: Coincident(g36,g13)
    c: Coincident(g36,g20)
    c: Coincident(g37,g20)
    c: Coincident(g37,g30)
    c: Block(g30)
    c: Coincident(g38,g1)
    c: Coincident(g38,g2)
    c: Coincident(g39,g1)
    c: Coincident(g39,g2)
    c: Coincident(g40,g3)
    c: Coincident(g40,g4)
    c: Coincident(g41,g3)
    c: Coincident(g41,g4)
    c: Coincident(g42,g5)
    c: Coincident(g42,g6)
    c: Coincident(g43,g5)
    c: Coincident(g43,g6)
    c: Coincident(g44,g7)
    c: Coincident(g44,g8)
    c: Coincident(g45,g7)
    c: Coincident(g45,g8)
    c: Distance(g30) = 256
    c: Distance(g33) = 100
FEATURE [Part::Extrusion] Extrude002
  Base = -> Sketch001
  Dir = (1,0,0)
  DirMode = 2
  FaceMakerClass = Part::FaceMakerBullseye
  LengthFwd = 8
  LengthRev = 0
  Solid = true
  Symmetric = false
FEATURE [Sketcher::SketchObject] Sketch002
  FullyConstrained = true
  sketch-geometry (20):
    g0: LineSegment StartX=-2.77179 StartY=-200.304 StartZ=0 EndX=5.22821 EndY=-200.304 EndZ=0
    g1: LineSegment StartX=5.22821 StartY=-200.304 StartZ=0 EndX=5.22821 EndY=-197.304 EndZ=0
    g2: LineSegment StartX=-2.77179 StartY=-200.304 StartZ=0 EndX=-2.77179 EndY=-197.304 EndZ=0
    g3: LineSegment StartX=5.22821 StartY=-197.304 StartZ=0 EndX=8.22821 EndY=-197.304 EndZ=0
    g4: LineSegment StartX=-2.77179 StartY=-197.304 StartZ=0 EndX=-5.77179 EndY=-197.304 EndZ=0
    g5: LineSegment StartX=19.2282 StartY=-203.304 StartZ=0 EndX=19.2282 EndY=-206.304 EndZ=0
    g6: LineSegment StartX=-16.7718 StartY=-203.304 StartZ=0 EndX=-16.7718 EndY=-206.304 EndZ=0
    g7: LineSegment StartX=-16.7718 StartY=-206.304 StartZ=0 EndX=19.2282 EndY=-206.304 EndZ=0
    g8: Circle CenterX=-16.7718 CenterY=-203.304 CenterZ=0 NormalX=0 NormalY=0 NormalZ=1 AngleXU=0 Radius=1
    g9: Circle CenterX=-5.77179 CenterY=-203.304 CenterZ=0 NormalX=0 NormalY=0 NormalZ=1 AngleXU=0 Radius=1
    g10: Circle CenterX=-5.77179 CenterY=-197.304 CenterZ=0 NormalX=0 NormalY=0 NormalZ=1 AngleXU=0 Radius=1
    g11: BSplineCurve PolesCount=3 KnotsCount=2 Degree=2 IsPeriodic=0
    g12: GeomPoint X=-16.7718 Y=-203.304 Z=0
    g13: GeomPoint X=-5.77179 Y=-197.304 Z=0
    g14: Circle CenterX=19.2282 CenterY=-203.304 CenterZ=0 NormalX=0 NormalY=0 NormalZ=1 AngleXU=0 Radius=1
    g15: Circle CenterX=8.22821 CenterY=-203.304 CenterZ=0 NormalX=0 NormalY=0 NormalZ=1 AngleXU=0 Radius=1
    g16: Circle CenterX=8.22821 CenterY=-197.304 CenterZ=0 NormalX=0 NormalY=0 NormalZ=1 AngleXU=0 Radius=1
    g17: BSplineCurve PolesCount=3 KnotsCount=2 Degree=2 IsPeriodic=0
    g18: GeomPoint X=19.2282 Y=-203.304 Z=0
    g19: GeomPoint X=8.22821 Y=-197.304 Z=0
  constraints (41):
    c: Horizontal(g0)
    c: Distance(g0) = 8
    c: Coincident(g1,g0)
    c: Vertical(g1)
    c: Distance(g1) = 3
    c: Coincident(g2,g0)
    c: Vertical(g2)
    c: Distance(g2) = 3
    c: Coincident(g3,g1)
    c: Horizontal(g3)
    c: Distance(g3) = 3
    c: Coincident(g4,g2)
    c: Horizontal(g4)
    c: Distance(g4) = 3
    c: Vertical(g5)
    c: Vertical(g6)
    c: Coincident(g7,g6)
    c: Coincident(g7,g5)
    c: Weight(g8) = 1
    c: Equal(g8,g9)
    c: Equal(g8,g10)
    c: Coincident(g11,g4)
    c: InternalAlignment(g8,g11)
    c: InternalAlignment(g9,g11)
    c: InternalAlignment(g10,g11)
    c: InternalAlignment(g12,g11)
    c: InternalAlignment(g13,g11)
    c: Coincident(g17,g5)
    c: Weight(g14) = 1
    c: Equal(g14,g15)
    c: Equal(g14,g16)
    c: Coincident(g17,g3)
    c: InternalAlignment(g14,g17)
    c: InternalAlignment(g15,g17)
    c: InternalAlignment(g16,g17)
    c: InternalAlignment(g18,g17)
    c: InternalAlignment(g19,g17)
    c: Block(g7)
    c: Block(g17)
    c: Block(g11)
    c: Block(g6)
FEATURE [Part::Extrusion] Extrude003
  Base = -> Sketch002
  Dir = (0,0,1)
  DirMode = 2
  FaceMakerClass = Part::FaceMakerBullseye
  LengthFwd = 260
  LengthRev = 0
  Solid = true
  Symmetric = false
FEATURE [Sketcher::SketchObject] Sketch003
  FullyConstrained = false
  sketch-geometry (393):
    g0: LineSegment StartX=-42.9272 StartY=136.221 StartZ=0 EndX=-42.9272 EndY=-103.779 EndZ=0
    g1: LineSegment StartX=407.073 StartY=136.221 StartZ=0 EndX=407.073 EndY=-103.779 EndZ=0
    g2: ArcOfCircle CenterX=-26.9272 CenterY=-83.7794 CenterZ=0 NormalX=0 NormalY=0 NormalZ=1 AngleXU=0 Radius=8 StartAngle=3.14159 EndAngle=6.28319
    g3: ArcOfCircle CenterX=391.073 CenterY=-83.7794 CenterZ=0 NormalX=0 NormalY=0 NormalZ=1 AngleXU=0 Radius=8 StartAngle=3.14159 EndAngle=6.28319
    g4: Circle CenterX=175.022 CenterY=27.0628 CenterZ=0 NormalX=0 NormalY=0 NormalZ=1 AngleXU=0 Radius=1
    g5: Circle CenterX=179.022 CenterY=24.8665 CenterZ=0 NormalX=0 NormalY=0 NormalZ=1 AngleXU=0 Radius=1
    g6: Circle CenterX=179.022 CenterY=27.0628 CenterZ=0 NormalX=0 NormalY=0 NormalZ=1 AngleXU=0 Radius=1
    g7: BSplineCurve PolesCount=3 KnotsCount=2 Degree=2 IsPeriodic=0
    g8: GeomPoint X=175.022 Y=27.0628 Z=0
    g9: GeomPoint X=179.022 Y=27.0628 Z=0
    g10: Circle CenterX=189.124 CenterY=27.0628 CenterZ=0 NormalX=0 NormalY=0 NormalZ=1 AngleXU=0 Radius=1
    g11: Circle CenterX=185.124 CenterY=24.8665 CenterZ=0 NormalX=0 NormalY=0 NormalZ=1 AngleXU=0 Radius=1
    g12: Circle CenterX=185.124 CenterY=27.0628 CenterZ=0 NormalX=0 NormalY=0 NormalZ=1 AngleXU=0 Radius=1
    g13: BSplineCurve PolesCount=3 KnotsCount=2 Degree=2 IsPeriodic=0
    g14: GeomPoint X=189.124 Y=27.0628 Z=0
    g15: GeomPoint X=185.124 Y=27.0628 Z=0
    g16: Circle CenterX=175.022 CenterY=5.37834 CenterZ=0 NormalX=0 NormalY=0 NormalZ=1 AngleXU=0 Radius=1
    g17: Circle CenterX=179.022 CenterY=7.57463 CenterZ=0 NormalX=0 NormalY=0 NormalZ=1 AngleXU=0 Radius=1
    g18: Circle CenterX=179.022 CenterY=5.34704 CenterZ=0 NormalX=0 NormalY=0 NormalZ=1 AngleXU=0 Radius=1
    g19: BSplineCurve PolesCount=3 KnotsCount=2 Degree=2 IsPeriodic=0
    g20: GeomPoint X=175.022 Y=5.37834 Z=0
    g21: GeomPoint X=179.022 Y=5.34704 Z=0
    g22: Circle CenterX=189.124 CenterY=5.37834 CenterZ=0 NormalX=0 NormalY=0 NormalZ=1 AngleXU=0 Radius=1
    g23: Circle CenterX=185.124 CenterY=7.57463 CenterZ=0 NormalX=0 NormalY=0 NormalZ=1 AngleXU=0 Radius=1
    g24: Circle CenterX=185.124 CenterY=5.34704 CenterZ=0 NormalX=0 NormalY=0 NormalZ=1 AngleXU=0 Radius=1
    g25: BSplineCurve PolesCount=3 KnotsCount=2 Degree=2 IsPeriodic=0
    g26: GeomPoint X=189.124 Y=5.37834 Z=0
    g27: GeomPoint X=185.124 Y=5.34704 Z=0
    g28: Circle CenterX=165.871 CenterY=18.1458 CenterZ=0 NormalX=0 NormalY=0 NormalZ=1 AngleXU=0 Radius=1
    g29: Circle CenterX=169.377 CenterY=16.2206 CenterZ=0 NormalX=0 NormalY=0 NormalZ=1 AngleXU=0 Radius=1
    g30: Circle CenterX=165.871 CenterY=14.2954 CenterZ=0 NormalX=0 NormalY=0 NormalZ=1 AngleXU=0 Radius=1
    g31: BSplineCurve PolesCount=3 KnotsCount=2 Degree=2 IsPeriodic=0
    g32: GeomPoint X=165.871 Y=18.1458 Z=0
    g33: GeomPoint X=165.871 Y=14.2954 Z=0
    g34: Circle CenterX=198.275 CenterY=18.1458 CenterZ=0 NormalX=0 NormalY=0 NormalZ=1 AngleXU=0 Radius=1
    g35: Circle CenterX=194.768 CenterY=16.2206 CenterZ=0 NormalX=0 NormalY=0 NormalZ=1 AngleXU=0 Radius=1
    g36: Circle CenterX=198.275 CenterY=14.2954 CenterZ=0 NormalX=0 NormalY=0 NormalZ=1 AngleXU=0 Radius=1
    g37: BSplineCurve PolesCount=3 KnotsCount=2 Degree=2 IsPeriodic=0
    g38: GeomPoint X=198.275 Y=18.1458 Z=0
    g39: GeomPoint X=198.275 Y=14.2954 Z=0
    g40: LineSegment StartX=407.073 StartY=-103.779 StartZ=0 EndX=-42.9272 EndY=-103.779 EndZ=0
    g41: Circle CenterX=125.607 CenterY=54.1951 CenterZ=0 NormalX=0 NormalY=0 NormalZ=1 AngleXU=0 Radius=1
    g42: Circle CenterX=139.632 CenterY=46.4944 CenterZ=0 NormalX=0 NormalY=0 NormalZ=1 AngleXU=0 Radius=1
    g43: Circle CenterX=127.326 CenterY=56.7187 CenterZ=0 NormalX=0 NormalY=0 NormalZ=1 AngleXU=0 Radius=1
    g44: BSplineCurve PolesCount=3 KnotsCount=2 Degree=2 IsPeriodic=0
    g45: GeomPoint X=125.607 Y=54.1951 Z=0
    g46: GeomPoint X=127.326 Y=56.7187 Z=0
    g47: Circle CenterX=236.821 CenterY=56.7187 CenterZ=0 NormalX=0 NormalY=0 NormalZ=1 AngleXU=0 Radius=1
    g48: Circle CenterX=224.513 CenterY=46.4944 CenterZ=0 NormalX=0 NormalY=0 NormalZ=1 AngleXU=0 Radius=1
    g49: Circle CenterX=238.538 CenterY=54.1951 CenterZ=0 NormalX=0 NormalY=0 NormalZ=1 AngleXU=0 Radius=1
    g50: BSplineCurve PolesCount=3 KnotsCount=2 Degree=2 IsPeriodic=0
    g51: GeomPoint X=236.821 Y=56.7187 Z=0
    g52: GeomPoint X=238.538 Y=54.1951 Z=0
    g53: Circle CenterX=238.538 CenterY=-21.7539 CenterZ=0 NormalX=0 NormalY=0 NormalZ=1 AngleXU=0 Radius=1
    g54: Circle CenterX=224.513 CenterY=-14.0532 CenterZ=0 NormalX=0 NormalY=0 NormalZ=1 AngleXU=0 Radius=1
    g55: Circle CenterX=236.821 CenterY=-24.2775 CenterZ=0 NormalX=0 NormalY=0 NormalZ=1 AngleXU=0 Radius=1
    g56: BSplineCurve PolesCount=3 KnotsCount=2 Degree=2 IsPeriodic=0
    g57: GeomPoint X=238.538 Y=-21.7539 Z=0
    g58: GeomPoint X=236.821 Y=-24.2775 Z=0
    g59: Circle CenterX=125.607 CenterY=-21.7539 CenterZ=0 NormalX=0 NormalY=0 NormalZ=1 AngleXU=0 Radius=1
    g60: Circle CenterX=139.632 CenterY=-14.0532 CenterZ=0 NormalX=0 NormalY=0 NormalZ=1 AngleXU=0 Radius=1
    g61: Circle CenterX=127.325 CenterY=-24.2775 CenterZ=0 NormalX=0 NormalY=0 NormalZ=1 AngleXU=0 Radius=1
    g62: BSplineCurve PolesCount=3 KnotsCount=2 Degree=2 IsPeriodic=0
    g63: GeomPoint X=125.607 Y=-21.7539 Z=0
    g64: GeomPoint X=127.325 Y=-24.2775 Z=0
    g65: Circle CenterX=302.996 CenterY=111.695 CenterZ=0 NormalX=0 NormalY=0 NormalZ=1 AngleXU=0 Radius=1
    g66: Circle CenterX=306.073 CenterY=114.251 CenterZ=0 NormalX=0 NormalY=0 NormalZ=1 AngleXU=0 Radius=1
    g67: Circle CenterX=306.073 CenterY=110.251 CenterZ=0 NormalX=0 NormalY=0 NormalZ=1 AngleXU=0 Radius=1
    g68: BSplineCurve PolesCount=3 KnotsCount=2 Degree=2 IsPeriodic=0
    g69: GeomPoint X=302.996 Y=111.695 Z=0
    g70: GeomPoint X=306.073 Y=110.251 Z=0
    g71: Circle CenterX=306.073 CenterY=95.2763 CenterZ=0 NormalX=0 NormalY=0 NormalZ=1 AngleXU=0 Radius=1
    g72: Circle CenterX=306.073 CenterY=91.2763 CenterZ=0 NormalX=0 NormalY=0 NormalZ=1 AngleXU=0 Radius=1
    g73: Circle CenterX=302.567 CenterY=89.3511 CenterZ=0 NormalX=0 NormalY=0 NormalZ=1 AngleXU=0 Radius=1
    g74: BSplineCurve PolesCount=3 KnotsCount=2 Degree=2 IsPeriodic=0
    g75: GeomPoint X=306.073 Y=95.2763 Z=0
    g76: GeomPoint X=302.567 Y=89.3511 Z=0
    g77: LineSegment StartX=306.073 StartY=110.251 StartZ=0 EndX=306.073 EndY=95.2763 EndZ=0
    g78: LineSegment StartX=302.996 StartY=111.695 StartZ=0 EndX=236.821 EndY=56.7187 EndZ=0
    g79: LineSegment StartX=238.538 StartY=54.1951 StartZ=0 EndX=302.567 EndY=89.3511 EndZ=0
    g80: Circle CenterX=61.1496 CenterY=111.695 CenterZ=0 NormalX=0 NormalY=0 NormalZ=1 AngleXU=0 Radius=1
    g81: Circle CenterX=58.0728 CenterY=114.251 CenterZ=0 NormalX=0 NormalY=0 NormalZ=1 AngleXU=0 Radius=1
    g82: Circle CenterX=58.0728 CenterY=110.251 CenterZ=0 NormalX=0 NormalY=0 NormalZ=1 AngleXU=0 Radius=1
    g83: BSplineCurve PolesCount=3 KnotsCount=2 Degree=2 IsPeriodic=0
    g84: GeomPoint X=61.1496 Y=111.695 Z=0
    g85: GeomPoint X=58.0728 Y=110.251 Z=0
    g86: Circle CenterX=61.5791 CenterY=89.3511 CenterZ=0 NormalX=0 NormalY=0 NormalZ=1 AngleXU=0 Radius=1
    g87: Circle CenterX=58.0728 CenterY=91.2763 CenterZ=0 NormalX=0 NormalY=0 NormalZ=1 AngleXU=0 Radius=1
    g88: Circle CenterX=58.0728 CenterY=95.2763 CenterZ=0 NormalX=0 NormalY=0 NormalZ=1 AngleXU=0 Radius=1
    g89: BSplineCurve PolesCount=3 KnotsCount=2 Degree=2 IsPeriodic=0
    g90: GeomPoint X=61.5791 Y=89.3511 Z=0
    g91: GeomPoint X=58.0728 Y=95.2763 Z=0
    g92: LineSegment StartX=58.0728 StartY=110.251 StartZ=0 EndX=58.0728 EndY=95.2763 EndZ=0
    g93: LineSegment StartX=61.1496 StartY=111.695 StartZ=0 EndX=127.326 EndY=56.7187 EndZ=0
    g94: LineSegment StartX=125.607 StartY=54.1951 StartZ=0 EndX=61.5791 EndY=89.3511 EndZ=0
    g95: Circle CenterX=61.5791 CenterY=-56.9099 CenterZ=0 NormalX=0 NormalY=0 NormalZ=1 AngleXU=0 Radius=1
    g96: Circle CenterX=58.0728 CenterY=-58.8351 CenterZ=0 NormalX=0 NormalY=0 NormalZ=1 AngleXU=0 Radius=1
    g97: Circle CenterX=58.0728 CenterY=-62.8351 CenterZ=0 NormalX=0 NormalY=0 NormalZ=1 AngleXU=0 Radius=1
    g98: BSplineCurve PolesCount=3 KnotsCount=2 Degree=2 IsPeriodic=0
    g99: GeomPoint X=61.5791 Y=-56.9099 Z=0
    g100: GeomPoint X=58.0728 Y=-62.8351 Z=0
    g101: Circle CenterX=58.0728 CenterY=-77.8102 CenterZ=0 NormalX=0 NormalY=0 NormalZ=1 AngleXU=0 Radius=1
    g102: Circle CenterX=58.0728 CenterY=-81.8102 CenterZ=0 NormalX=0 NormalY=0 NormalZ=1 AngleXU=0 Radius=1
    g103: Circle CenterX=61.1496 CenterY=-79.2541 CenterZ=0 NormalX=0 NormalY=0 NormalZ=1 AngleXU=0 Radius=1
    g104: BSplineCurve PolesCount=3 KnotsCount=2 Degree=2 IsPeriodic=0
    g105: GeomPoint X=58.0728 Y=-77.8102 Z=0
    g106: GeomPoint X=61.1496 Y=-79.2541 Z=0
    g107: LineSegment StartX=58.0728 StartY=-62.8351 StartZ=0 EndX=58.0728 EndY=-77.8102 EndZ=0
    g108: LineSegment StartX=61.1496 StartY=-79.2541 StartZ=0 EndX=127.325 EndY=-24.2775 EndZ=0
    g109: LineSegment StartX=125.607 StartY=-21.7539 StartZ=0 EndX=61.5791 EndY=-56.9099 EndZ=0
    g110: Circle CenterX=302.567 CenterY=-56.9099 CenterZ=0 NormalX=0 NormalY=0 NormalZ=1 AngleXU=0 Radius=1
    g111: Circle CenterX=306.073 CenterY=-58.8351 CenterZ=0 NormalX=0 NormalY=0 NormalZ=1 AngleXU=0 Radius=1
    g112: Circle CenterX=306.073 CenterY=-62.8351 CenterZ=0 NormalX=0 NormalY=0 NormalZ=1 AngleXU=0 Radius=1
    g113: BSplineCurve PolesCount=3 KnotsCount=2 Degree=2 IsPeriodic=0
    g114: GeomPoint X=302.567 Y=-56.9099 Z=0
    g115: GeomPoint X=306.073 Y=-62.8351 Z=0
    g116: Circle CenterX=302.996 CenterY=-79.2541 CenterZ=0 NormalX=0 NormalY=0 NormalZ=1 AngleXU=0 Radius=1
    g117: Circle CenterX=306.073 CenterY=-81.8102 CenterZ=0 NormalX=0 NormalY=0 NormalZ=1 AngleXU=0 Radius=1
    g118: Circle CenterX=306.073 CenterY=-77.8102 CenterZ=0 NormalX=0 NormalY=0 NormalZ=1 AngleXU=0 Radius=1
    g119: BSplineCurve PolesCount=3 KnotsCount=2 Degree=2 IsPeriodic=0
    g120: GeomPoint X=302.996 Y=-79.2541 Z=0
    g121: GeomPoint X=306.073 Y=-77.8102 Z=0
    g122: LineSegment StartX=306.073 StartY=-62.8351 StartZ=0 EndX=306.073 EndY=-77.8102 EndZ=0
    g123: LineSegment StartX=302.996 StartY=-79.2541 StartZ=0 EndX=236.821 EndY=-24.2775 EndZ=0
    g124: LineSegment StartX=238.538 StartY=-21.7539 StartZ=0 EndX=302.567 EndY=-56.9099 EndZ=0
    g125: Circle CenterX=61.6457 CenterY=-88.8112 CenterZ=0 NormalX=0 NormalY=0 NormalZ=1 AngleXU=0 Radius=1
    g126: Circle CenterX=58.0728 CenterY=-91.7794 CenterZ=0 NormalX=0 NormalY=0 NormalZ=1 AngleXU=0 Radius=1
    g127: Circle CenterX=63.9135 CenterY=-91.7794 CenterZ=0 NormalX=0 NormalY=0 NormalZ=1 AngleXU=0 Radius=1
    g128: BSplineCurve PolesCount=3 KnotsCount=2 Degree=2 IsPeriodic=0
    g129: GeomPoint X=61.6457 Y=-88.8112 Z=0
    g130: GeomPoint X=63.9135 Y=-91.7794 Z=0
    g131: Circle CenterX=179.022 CenterY=-85.8163 CenterZ=0 NormalX=0 NormalY=0 NormalZ=1 AngleXU=0 Radius=1
    g132: Circle CenterX=179.022 CenterY=-91.7794 CenterZ=0 NormalX=0 NormalY=0 NormalZ=1 AngleXU=0 Radius=1
    g133: Circle CenterX=171.895 CenterY=-91.7794 CenterZ=0 NormalX=0 NormalY=0 NormalZ=1 AngleXU=0 Radius=1
    g134: BSplineCurve PolesCount=3 KnotsCount=2 Degree=2 IsPeriodic=0
    g135: GeomPoint X=179.022 Y=-85.8163 Z=0
    g136: GeomPoint X=171.895 Y=-91.7794 Z=0
    g137: Circle CenterX=185.124 CenterY=-86.2028 CenterZ=0 NormalX=0 NormalY=0 NormalZ=1 AngleXU=0 Radius=1
    g138: Circle CenterX=185.124 CenterY=-91.7794 CenterZ=0 NormalX=0 NormalY=0 NormalZ=1 AngleXU=0 Radius=1
    g139: Circle CenterX=191.747 CenterY=-91.7794 CenterZ=0 NormalX=0 NormalY=0 NormalZ=1 AngleXU=0 Radius=1
    g140: BSplineCurve PolesCount=3 KnotsCount=2 Degree=2 IsPeriodic=0
    g141: GeomPoint X=185.124 Y=-86.2028 Z=0
    g142: GeomPoint X=191.747 Y=-91.7794 Z=0
    g143: Circle CenterX=299.888 CenterY=-86.6413 CenterZ=0 NormalX=0 NormalY=0 NormalZ=1 AngleXU=0 Radius=1
    g144: Circle CenterX=306.073 CenterY=-91.7794 CenterZ=0 NormalX=0 NormalY=0 NormalZ=1 AngleXU=0 Radius=1
    g145: Circle CenterX=298.776 CenterY=-91.7794 CenterZ=0 NormalX=0 NormalY=0 NormalZ=1 AngleXU=0 Radius=1
    g146: BSplineCurve PolesCount=3 KnotsCount=2 Degree=2 IsPeriodic=0
    g147: GeomPoint X=299.888 Y=-86.6413 Z=0
    g148: GeomPoint X=298.776 Y=-91.7794 Z=0
    g149: LineSegment StartX=189.124 StartY=5.37834 StartZ=0 EndX=299.888 EndY=-86.6413 EndZ=0
    g150: LineSegment StartX=298.776 StartY=-91.7794 StartZ=0 EndX=191.747 EndY=-91.7794 EndZ=0
    g151: LineSegment StartX=185.124 StartY=-86.2028 StartZ=0 EndX=185.124 EndY=5.34704 EndZ=0
    g152: LineSegment StartX=179.022 StartY=5.34704 StartZ=0 EndX=179.022 EndY=-85.8163 EndZ=0
    g153: LineSegment StartX=171.895 StartY=-91.7794 StartZ=0 EndX=63.9135 EndY=-91.7794 EndZ=0
    g154: LineSegment StartX=61.6457 StartY=-88.8112 StartZ=0 EndX=175.022 EndY=5.37834 EndZ=0
    g155: Circle CenterX=302.073 CenterY=124.221 CenterZ=0 NormalX=0 NormalY=0 NormalZ=1 AngleXU=0 Radius=1
    g156: Circle CenterX=306.073 CenterY=124.221 CenterZ=0 NormalX=0 NormalY=0 NormalZ=1 AngleXU=0 Radius=1
    g157: Circle CenterX=302.996 CenterY=121.665 CenterZ=0 NormalX=0 NormalY=0 NormalZ=1 AngleXU=0 Radius=1
    g158: BSplineCurve PolesCount=3 KnotsCount=2 Degree=2 IsPeriodic=0
    g159: GeomPoint X=302.073 Y=124.221 Z=0
    g160: GeomPoint X=302.996 Y=121.665 Z=0
    g161: Circle CenterX=189.124 CenterY=124.221 CenterZ=0 NormalX=0 NormalY=0 NormalZ=1 AngleXU=0 Radius=1
    g162: Circle CenterX=185.124 CenterY=124.221 CenterZ=0 NormalX=0 NormalY=0 NormalZ=1 AngleXU=0 Radius=1
    g163: Circle CenterX=185.124 CenterY=120.221 CenterZ=0 NormalX=0 NormalY=0 NormalZ=1 AngleXU=0 Radius=1
    g164: BSplineCurve PolesCount=3 KnotsCount=2 Degree=2 IsPeriodic=0
    g165: GeomPoint X=189.124 Y=124.221 Z=0
    g166: GeomPoint X=185.124 Y=120.221 Z=0
    g167: Circle CenterX=175.022 CenterY=124.221 CenterZ=0 NormalX=0 NormalY=0 NormalZ=1 AngleXU=0 Radius=1
    g168: Circle CenterX=179.022 CenterY=124.221 CenterZ=0 NormalX=0 NormalY=0 NormalZ=1 AngleXU=0 Radius=1
    g169: Circle CenterX=179.022 CenterY=120.221 CenterZ=0 NormalX=0 NormalY=0 NormalZ=1 AngleXU=0 Radius=1
    g170: BSplineCurve PolesCount=3 KnotsCount=2 Degree=2 IsPeriodic=0
    g171: GeomPoint X=175.022 Y=124.221 Z=0
    g172: GeomPoint X=179.022 Y=120.221 Z=0
    g173: Circle CenterX=62.0728 CenterY=124.221 CenterZ=0 NormalX=0 NormalY=0 NormalZ=1 AngleXU=0 Radius=1
    g174: Circle CenterX=58.0728 CenterY=124.221 CenterZ=0 NormalX=0 NormalY=0 NormalZ=1 AngleXU=0 Radius=1
    g175: Circle CenterX=61.1496 CenterY=121.665 CenterZ=0 NormalX=0 NormalY=0 NormalZ=1 AngleXU=0 Radius=1
    g176: BSplineCurve PolesCount=3 KnotsCount=2 Degree=2 IsPeriodic=0
    g177: GeomPoint X=62.0728 Y=124.221 Z=0
    g178: GeomPoint X=61.1496 Y=121.665 Z=0
    g179: LineSegment StartX=62.0728 StartY=124.221 StartZ=0 EndX=175.022 EndY=124.221 EndZ=0
    g180: LineSegment StartX=179.022 StartY=120.221 StartZ=0 EndX=179.022 EndY=27.0628 EndZ=0
    g181: LineSegment StartX=185.124 StartY=27.0628 StartZ=0 EndX=185.124 EndY=120.221 EndZ=0
    g182: LineSegment StartX=302.996 StartY=121.665 StartZ=0 EndX=189.124 EndY=27.0628 EndZ=0
    g183: LineSegment StartX=175.022 StartY=27.0628 StartZ=0 EndX=61.1496 EndY=121.665 EndZ=0
    g184: Circle CenterX=61.5791 CenterY=75.4095 CenterZ=0 NormalX=0 NormalY=0 NormalZ=1 AngleXU=0 Radius=1
    g185: Circle CenterX=58.0728 CenterY=77.3346 CenterZ=0 NormalX=0 NormalY=0 NormalZ=1 AngleXU=0 Radius=1
    g186: Circle CenterX=58.0728 CenterY=73.3346 CenterZ=0 NormalX=0 NormalY=0 NormalZ=1 AngleXU=0 Radius=1
    g187: BSplineCurve PolesCount=3 KnotsCount=2 Degree=2 IsPeriodic=0
    g188: GeomPoint X=61.5791 Y=75.4095 Z=0
    g189: GeomPoint X=58.0728 Y=73.3346 Z=0
    g190: Circle CenterX=58.0728 CenterY=-40.8935 CenterZ=0 NormalX=0 NormalY=0 NormalZ=1 AngleXU=0 Radius=1
    g191: Circle CenterX=58.0728 CenterY=-44.8935 CenterZ=0 NormalX=0 NormalY=0 NormalZ=1 AngleXU=0 Radius=1
    g192: Circle CenterX=61.5791 CenterY=-42.9683 CenterZ=0 NormalX=0 NormalY=0 NormalZ=1 AngleXU=0 Radius=1
    g193: BSplineCurve PolesCount=3 KnotsCount=2 Degree=2 IsPeriodic=0
    g194: GeomPoint X=58.0728 Y=-40.8935 Z=0
    g195: GeomPoint X=61.5791 Y=-42.9683 Z=0
    g196: LineSegment StartX=61.5791 StartY=-42.9683 StartZ=0 EndX=165.871 EndY=14.2954 EndZ=0
    g197: LineSegment StartX=165.871 StartY=18.1458 StartZ=0 EndX=61.5791 EndY=75.4095 EndZ=0
    g198: LineSegment StartX=58.0728 StartY=73.3346 StartZ=0 EndX=58.0728 EndY=-40.8935 EndZ=0
    g199: Circle CenterX=302.567 CenterY=-42.9683 CenterZ=0 NormalX=0 NormalY=0 NormalZ=1 AngleXU=0 Radius=1
    g200: Circle CenterX=306.073 CenterY=-44.8935 CenterZ=0 NormalX=0 NormalY=0 NormalZ=1 AngleXU=0 Radius=1
    g201: Circle CenterX=306.073 CenterY=-40.8935 CenterZ=0 NormalX=0 NormalY=0 NormalZ=1 AngleXU=0 Radius=1
    g202: BSplineCurve PolesCount=3 KnotsCount=2 Degree=2 IsPeriodic=0
    g203: GeomPoint X=302.567 Y=-42.9683 Z=0
    g204: GeomPoint X=306.073 Y=-40.8935 Z=0
    g205: Circle CenterX=306.073 CenterY=73.3346 CenterZ=0 NormalX=0 NormalY=0 NormalZ=1 AngleXU=0 Radius=1
    g206: Circle CenterX=306.073 CenterY=77.3346 CenterZ=0 NormalX=0 NormalY=0 NormalZ=1 AngleXU=0 Radius=1
    g207: Circle CenterX=302.567 CenterY=75.4095 CenterZ=0 NormalX=0 NormalY=0 NormalZ=1 AngleXU=0 Radius=1
    g208: BSplineCurve PolesCount=3 KnotsCount=2 Degree=2 IsPeriodic=0
    g209: GeomPoint X=306.073 Y=73.3346 Z=0
    g210: GeomPoint X=302.567 Y=75.4095 Z=0
    g211: LineSegment StartX=302.567 StartY=-42.9683 StartZ=0 EndX=198.275 EndY=14.2954 EndZ=0
    g212: LineSegment StartX=198.275 StartY=18.1458 StartZ=0 EndX=302.567 EndY=75.4095 EndZ=0
    g213: LineSegment StartX=306.073 StartY=73.3346 StartZ=0 EndX=306.073 EndY=-40.8935 EndZ=0
    g214: LineSegment StartX=322.073 StartY=105.865 StartZ=0 EndX=328.643 EndY=105.865 EndZ=0
    g215: LineSegment StartX=318.073 StartY=120.221 StartZ=0 EndX=318.073 EndY=109.865 EndZ=0
    g216: LineSegment StartX=336.157 StartY=107.779 StartZ=0 EndX=362.567 EndY=122.294 EndZ=0
    g217: Circle CenterX=362.073 CenterY=124.221 CenterZ=0 NormalX=0 NormalY=0 NormalZ=1 AngleXU=0 Radius=1
    g218: Circle CenterX=366.073 CenterY=124.221 CenterZ=0 NormalX=0 NormalY=0 NormalZ=1 AngleXU=0 Radius=1
    g219: Circle CenterX=362.567 CenterY=122.294 CenterZ=0 NormalX=0 NormalY=0 NormalZ=1 AngleXU=0 Radius=1
    g220: BSplineCurve PolesCount=3 KnotsCount=2 Degree=2 IsPeriodic=0
    g221: GeomPoint X=362.073 Y=124.221 Z=0
    g222: GeomPoint X=362.567 Y=122.294 Z=0
    g223: Circle CenterX=322.073 CenterY=124.221 CenterZ=0 NormalX=0 NormalY=0 NormalZ=1 AngleXU=0 Radius=1
    g224: Circle CenterX=318.073 CenterY=124.221 CenterZ=0 NormalX=0 NormalY=0 NormalZ=1 AngleXU=0 Radius=1
    g225: Circle CenterX=318.073 CenterY=120.221 CenterZ=0 NormalX=0 NormalY=0 NormalZ=1 AngleXU=0 Radius=1
    g226: BSplineCurve PolesCount=3 KnotsCount=2 Degree=2 IsPeriodic=0
    g227: GeomPoint X=322.073 Y=124.221 Z=0
    g228: GeomPoint X=318.073 Y=120.221 Z=0
    g229: Circle CenterX=322.073 CenterY=105.865 CenterZ=0 NormalX=0 NormalY=0 NormalZ=1 AngleXU=0 Radius=1
    g230: Circle CenterX=318.073 CenterY=105.865 CenterZ=0 NormalX=0 NormalY=0 NormalZ=1 AngleXU=0 Radius=1
    g231: Circle CenterX=318.073 CenterY=109.865 CenterZ=0 NormalX=0 NormalY=0 NormalZ=1 AngleXU=0 Radius=1
    g232: BSplineCurve PolesCount=3 KnotsCount=2 Degree=2 IsPeriodic=0
    g233: GeomPoint X=322.073 Y=105.865 Z=0
    g234: GeomPoint X=318.073 Y=109.865 Z=0
    g235: Circle CenterX=336.157 CenterY=107.779 CenterZ=0 NormalX=0 NormalY=0 NormalZ=1 AngleXU=0 Radius=1
    g236: Circle CenterX=332.651 CenterY=105.853 CenterZ=0 NormalX=0 NormalY=0 NormalZ=1 AngleXU=0 Radius=1
    g237: Circle CenterX=328.643 CenterY=105.865 CenterZ=0 NormalX=0 NormalY=0 NormalZ=1 AngleXU=0 Radius=1
    g238: BSplineCurve PolesCount=3 KnotsCount=2 Degree=2 IsPeriodic=0
    g239: GeomPoint X=336.157 Y=107.779 Z=0
    g240: GeomPoint X=328.643 Y=105.865 Z=0
    g241: LineSegment StartX=322.073 StartY=124.221 StartZ=0 EndX=362.073 EndY=124.221 EndZ=0
    g242: Circle CenterX=371.567 CenterY=-80.8644 CenterZ=0 NormalX=0 NormalY=0 NormalZ=1 AngleXU=0 Radius=1
    g243: Circle CenterX=375.073 CenterY=-82.7896 CenterZ=0 NormalX=0 NormalY=0 NormalZ=1 AngleXU=0 Radius=1
    g244: Circle CenterX=375.073 CenterY=-78.7896 CenterZ=0 NormalX=0 NormalY=0 NormalZ=1 AngleXU=0 Radius=1
    g245: BSplineCurve PolesCount=3 KnotsCount=2 Degree=2 IsPeriodic=0
    g246: GeomPoint X=371.567 Y=-80.8644 Z=0
    g247: GeomPoint X=375.073 Y=-78.7896 Z=0
    g248: Circle CenterX=321.579 CenterY=-53.4075 CenterZ=0 NormalX=0 NormalY=0 NormalZ=1 AngleXU=0 Radius=1
    g249: Circle CenterX=318.073 CenterY=-51.4823 CenterZ=0 NormalX=0 NormalY=0 NormalZ=1 AngleXU=0 Radius=1
    g250: Circle CenterX=318.073 CenterY=-47.4805 CenterZ=0 NormalX=0 NormalY=0 NormalZ=1 AngleXU=0 Radius=1
    g251: BSplineCurve PolesCount=3 KnotsCount=2 Degree=2 IsPeriodic=0
    g252: GeomPoint X=321.579 Y=-53.4075 Z=0
    g253: GeomPoint X=318.073 Y=-47.4805 Z=0
    g254: LineSegment StartX=371.567 StartY=-80.8644 StartZ=0 EndX=321.579 EndY=-53.4075 EndZ=0
    g255: Circle CenterX=321.579 CenterY=-67.3492 CenterZ=0 NormalX=0 NormalY=0 NormalZ=1 AngleXU=0 Radius=1
    g256: Circle CenterX=318.073 CenterY=-65.424 CenterZ=0 NormalX=0 NormalY=0 NormalZ=1 AngleXU=0 Radius=1
    g257: Circle CenterX=318.073 CenterY=-69.424 CenterZ=0 NormalX=0 NormalY=0 NormalZ=1 AngleXU=0 Radius=1
    g258: BSplineCurve PolesCount=3 KnotsCount=2 Degree=2 IsPeriodic=0
    g259: GeomPoint X=321.579 Y=-67.3492 Z=0
    g260: GeomPoint X=318.073 Y=-69.424 Z=0
    g261: Circle CenterX=362.567 CenterY=-89.8542 CenterZ=0 NormalX=0 NormalY=0 NormalZ=1 AngleXU=0 Radius=1
    g262: Circle CenterX=366.073 CenterY=-91.7794 CenterZ=0 NormalX=0 NormalY=0 NormalZ=1 AngleXU=0 Radius=1
    g263: Circle CenterX=362.073 CenterY=-91.7794 CenterZ=0 NormalX=0 NormalY=0 NormalZ=1 AngleXU=0 Radius=1
    g264: BSplineCurve PolesCount=3 KnotsCount=2 Degree=2 IsPeriodic=0
    g265: GeomPoint X=362.567 Y=-89.8542 Z=0
    g266: GeomPoint X=362.073 Y=-91.7794 Z=0
    g267: Circle CenterX=322.073 CenterY=-91.7794 CenterZ=0 NormalX=0 NormalY=0 NormalZ=1 AngleXU=0 Radius=1
    g268: Circle CenterX=318.073 CenterY=-91.7794 CenterZ=0 NormalX=0 NormalY=0 NormalZ=1 AngleXU=0 Radius=1
    g269: Circle CenterX=318.073 CenterY=-87.7794 CenterZ=0 NormalX=0 NormalY=0 NormalZ=1 AngleXU=0 Radius=1
    g270: BSplineCurve PolesCount=3 KnotsCount=2 Degree=2 IsPeriodic=0
    g271: GeomPoint X=322.073 Y=-91.7794 Z=0
    g272: GeomPoint X=318.073 Y=-87.7794 Z=0
    g273: LineSegment StartX=362.567 StartY=-89.8542 StartZ=0 EndX=321.579 EndY=-67.3492 EndZ=0
    g274: LineSegment StartX=318.073 StartY=-69.424 StartZ=0 EndX=318.073 EndY=-87.7794 EndZ=0
    g275: LineSegment StartX=322.073 StartY=-91.7794 StartZ=0 EndX=362.073 EndY=-91.7794 EndZ=0
    g276: Circle CenterX=2.07281 CenterY=124.221 CenterZ=0 NormalX=0 NormalY=0 NormalZ=1 AngleXU=0 Radius=1
    g277: Circle CenterX=1.57905 CenterY=122.295 CenterZ=0 NormalX=0 NormalY=0 NormalZ=1 AngleXU=0 Radius=1
    g278: BSplineCurve PolesCount=3 KnotsCount=2 Degree=2 IsPeriodic=0
    g279: GeomPoint X=2.07281 Y=124.221 Z=0
    g280: GeomPoint X=1.57905 Y=122.295 Z=0
    g281: Circle CenterX=42.0728 CenterY=124.221 CenterZ=0 NormalX=0 NormalY=0 NormalZ=1 AngleXU=0 Radius=1
    g282: Circle CenterX=46.0728 CenterY=124.221 CenterZ=0 NormalX=0 NormalY=0 NormalZ=1 AngleXU=0 Radius=1
    g283: Circle CenterX=46.0728 CenterY=120.221 CenterZ=0 NormalX=0 NormalY=0 NormalZ=1 AngleXU=0 Radius=1
    g284: BSplineCurve PolesCount=3 KnotsCount=2 Degree=2 IsPeriodic=0
    g285: GeomPoint X=42.0728 Y=124.221 Z=0
    g286: GeomPoint X=46.0728 Y=120.221 Z=0
    g287: Circle CenterX=46.0728 CenterY=109.865 CenterZ=0 NormalX=0 NormalY=0 NormalZ=1 AngleXU=0 Radius=1
    g288: Circle CenterX=46.0728 CenterY=105.865 CenterZ=0 NormalX=0 NormalY=0 NormalZ=1 AngleXU=0 Radius=1
    g289: Circle CenterX=42.0728 CenterY=105.865 CenterZ=0 NormalX=0 NormalY=0 NormalZ=1 AngleXU=0 Radius=1
    g290: BSplineCurve PolesCount=3 KnotsCount=2 Degree=2 IsPeriodic=0
    g291: GeomPoint X=46.0728 Y=109.865 Z=0
    g292: GeomPoint X=42.0728 Y=105.865 Z=0
    g293: Circle CenterX=35.5028 CenterY=105.865 CenterZ=0 NormalX=0 NormalY=0 NormalZ=1 AngleXU=0 Radius=1
    g294: Circle CenterX=31.5028 CenterY=105.865 CenterZ=0 NormalX=0 NormalY=0 NormalZ=1 AngleXU=0 Radius=1
    g295: Circle CenterX=27.9965 CenterY=107.79 CenterZ=0 NormalX=0 NormalY=0 NormalZ=1 AngleXU=0 Radius=1
    g296: BSplineCurve PolesCount=3 KnotsCount=2 Degree=2 IsPeriodic=0
    g297: GeomPoint X=35.5028 Y=105.865 Z=0
    g298: GeomPoint X=27.9965 Y=107.79 Z=0
    g299: LineSegment StartX=2.07281 StartY=124.221 StartZ=0 EndX=42.0728 EndY=124.221 EndZ=0
    g300: LineSegment StartX=46.0728 StartY=120.221 StartZ=0 EndX=46.0728 EndY=109.865 EndZ=0
    g301: LineSegment StartX=42.0728 StartY=105.865 StartZ=0 EndX=35.5028 EndY=105.865 EndZ=0
    g302: LineSegment StartX=27.9965 StartY=107.79 StartZ=0 EndX=1.57905 EndY=122.295 EndZ=0
    g303: Circle CenterX=42.5666 CenterY=-67.3492 CenterZ=0 NormalX=0 NormalY=0 NormalZ=1 AngleXU=0 Radius=1
    g304: Circle CenterX=46.0728 CenterY=-65.424 CenterZ=0 NormalX=0 NormalY=0 NormalZ=1 AngleXU=0 Radius=1
    g305: Circle CenterX=46.0728 CenterY=-69.424 CenterZ=0 NormalX=0 NormalY=0 NormalZ=1 AngleXU=0 Radius=1
    g306: BSplineCurve PolesCount=3 KnotsCount=2 Degree=2 IsPeriodic=0
    g307: GeomPoint X=42.5666 Y=-67.3492 Z=0
    g308: GeomPoint X=46.0728 Y=-69.424 Z=0
    g309: Circle CenterX=46.0728 CenterY=-87.7794 CenterZ=0 NormalX=0 NormalY=0 NormalZ=1 AngleXU=0 Radius=1
    g310: Circle CenterX=46.0728 CenterY=-91.7794 CenterZ=0 NormalX=0 NormalY=0 NormalZ=1 AngleXU=0 Radius=1
    g311: Circle CenterX=42.0728 CenterY=-91.7794 CenterZ=0 NormalX=0 NormalY=0 NormalZ=1 AngleXU=0 Radius=1
    g312: BSplineCurve PolesCount=3 KnotsCount=2 Degree=2 IsPeriodic=0
    g313: GeomPoint X=46.0728 Y=-87.7794 Z=0
    g314: GeomPoint X=42.0728 Y=-91.7794 Z=0
    g315: Circle CenterX=2.07281 CenterY=-91.7794 CenterZ=0 NormalX=0 NormalY=0 NormalZ=1 AngleXU=0 Radius=1
    g316: Circle CenterX=-1.92719 CenterY=-91.7794 CenterZ=0 NormalX=0 NormalY=0 NormalZ=1 AngleXU=0 Radius=1
    g317: Circle CenterX=1.57905 CenterY=-89.8542 CenterZ=0 NormalX=0 NormalY=0 NormalZ=1 AngleXU=0 Radius=1
    g318: BSplineCurve PolesCount=3 KnotsCount=2 Degree=2 IsPeriodic=0
    g319: GeomPoint X=2.07281 Y=-91.7794 Z=0
    g320: GeomPoint X=1.57905 Y=-89.8542 Z=0
    g321: LineSegment StartX=2.07281 StartY=-91.7794 StartZ=0 EndX=42.0728 EndY=-91.7794 EndZ=0
    g322: LineSegment StartX=46.0728 StartY=-87.7794 StartZ=0 EndX=46.0728 EndY=-69.424 EndZ=0
    g323: LineSegment StartX=42.5666 StartY=-67.3492 StartZ=0 EndX=1.57905 EndY=-89.8542 EndZ=0
    g324: Circle CenterX=322.073 CenterY=76.4095 CenterZ=0 NormalX=0 NormalY=0 NormalZ=1 AngleXU=0 Radius=4
    g325: BSplineCurve PolesCount=3 KnotsCount=2 Degree=2 IsPeriodic=0
    g326: GeomPoint X=318.073 Y=72.4095 Z=0
    g327: GeomPoint X=322.073 Y=76.4095 Z=0
    g328: Circle CenterX=375.073 CenterY=72.4095 CenterZ=0 NormalX=0 NormalY=0 NormalZ=1 AngleXU=0 Radius=1
    g329: Circle CenterX=375.073 CenterY=76.4095 CenterZ=0 NormalX=0 NormalY=0 NormalZ=1 AngleXU=0 Radius=1
    g330: Circle CenterX=371.073 CenterY=76.4095 CenterZ=0 NormalX=0 NormalY=0 NormalZ=1 AngleXU=0 Radius=1
    g331: BSplineCurve PolesCount=3 KnotsCount=2 Degree=2 IsPeriodic=0
    g332: GeomPoint X=375.073 Y=72.4095 Z=0
    g333: GeomPoint X=371.073 Y=76.4095 Z=0
    g334: LineSegment StartX=322.073 StartY=76.4095 StartZ=0 EndX=371.073 EndY=76.4095 EndZ=0
    g335: LineSegment StartX=318.073 StartY=72.4095 StartZ=0 EndX=318.073 EndY=-47.4805 EndZ=0
    g336: LineSegment StartX=375.073 StartY=72.4095 StartZ=0 EndX=375.073 EndY=-78.7896 EndZ=0
    g337: ArcOfCircle CenterX=-26.9272 CenterY=22.1087 CenterZ=0 NormalX=0 NormalY=0 NormalZ=1 AngleXU=0 Radius=4 StartAngle=5e-16 EndAngle=3.14159
    g338: LineSegment StartX=-22.9272 StartY=22.1087 StartZ=0 EndX=-18.9272 EndY=-83.7794 EndZ=0
    g339: LineSegment StartX=-34.9272 StartY=-83.7794 StartZ=0 EndX=-30.9272 EndY=22.1087 EndZ=0
    g340: ArcOfCircle CenterX=391.073 CenterY=22.1087 CenterZ=0 NormalX=0 NormalY=0 NormalZ=1 AngleXU=0 Radius=4 StartAngle=0 EndAngle=3.14159
    g341: LineSegment StartX=387.073 StartY=22.1087 StartZ=0 EndX=383.073 EndY=-83.7794 EndZ=0
    g342: LineSegment StartX=395.073 StartY=22.1087 StartZ=0 EndX=399.073 EndY=-83.7794 EndZ=0
    g343: Circle CenterX=-10.9272 CenterY=-78.7794 CenterZ=0 NormalX=0 NormalY=0 NormalZ=1 AngleXU=0 Radius=1
    g344: Circle CenterX=-10.9272 CenterY=-82.7794 CenterZ=0 NormalX=0 NormalY=0 NormalZ=1 AngleXU=0 Radius=1
    g345: Circle CenterX=-7.42095 CenterY=-80.8542 CenterZ=0 NormalX=0 NormalY=0 NormalZ=1 AngleXU=0 Radius=1
    g346: BSplineCurve PolesCount=3 KnotsCount=2 Degree=2 IsPeriodic=0
    g347: GeomPoint X=-10.9272 Y=-78.7794 Z=0
    g348: GeomPoint X=-7.42095 Y=-80.8542 Z=0
    g349: Circle CenterX=42.5666 CenterY=-53.4075 CenterZ=0 NormalX=0 NormalY=0 NormalZ=1 AngleXU=0 Radius=1
    g350: Circle CenterX=46.0728 CenterY=-51.4823 CenterZ=0 NormalX=0 NormalY=0 NormalZ=1 AngleXU=0 Radius=1
    g351: Circle CenterX=46.0728 CenterY=-47.4823 CenterZ=0 NormalX=0 NormalY=0 NormalZ=1 AngleXU=0 Radius=1
    g352: BSplineCurve PolesCount=3 KnotsCount=2 Degree=2 IsPeriodic=0
    g353: GeomPoint X=42.5666 Y=-53.4075 Z=0
    g354: GeomPoint X=46.0728 Y=-47.4823 Z=0
    g355: Circle CenterX=46.0728 CenterY=72.4095 CenterZ=0 NormalX=0 NormalY=0 NormalZ=1 AngleXU=0 Radius=1
    g356: Circle CenterX=46.0728 CenterY=76.4095 CenterZ=0 NormalX=0 NormalY=0 NormalZ=1 AngleXU=0 Radius=1
    g357: Circle CenterX=42.0728 CenterY=76.4095 CenterZ=0 NormalX=0 NormalY=0 NormalZ=1 AngleXU=0 Radius=1
    g358: BSplineCurve PolesCount=3 KnotsCount=2 Degree=2 IsPeriodic=0
    g359: GeomPoint X=46.0728 Y=72.4095 Z=0
    g360: GeomPoint X=42.0728 Y=76.4095 Z=0
    g361: Circle CenterX=-6.92718 CenterY=76.4095 CenterZ=0 NormalX=0 NormalY=0 NormalZ=1 AngleXU=0 Radius=1
    g362: Circle CenterX=-10.9272 CenterY=76.4095 CenterZ=0 NormalX=0 NormalY=0 NormalZ=1 AngleXU=0 Radius=1
    g363: Circle CenterX=-10.9272 CenterY=72.4095 CenterZ=0 NormalX=0 NormalY=0 NormalZ=1 AngleXU=0 Radius=1
    g364: BSplineCurve PolesCount=3 KnotsCount=2 Degree=2 IsPeriodic=0
    g365: GeomPoint X=-6.92718 Y=76.4095 Z=0
    g366: GeomPoint X=-10.9272 Y=72.4095 Z=0
    g367: LineSegment StartX=-10.9272 StartY=72.4095 StartZ=0 EndX=-10.9272 EndY=-78.7794 EndZ=0
    g368: LineSegment StartX=-7.42095 StartY=-80.8542 StartZ=0 EndX=42.5666 EndY=-53.4075 EndZ=0
    g369: LineSegment StartX=46.0728 StartY=-47.4823 StartZ=0 EndX=46.0728 EndY=72.4095 EndZ=0
    g370: LineSegment StartX=42.0728 StartY=76.4095 StartZ=0 EndX=-6.92719 EndY=76.4095 EndZ=0
    g371: LineSegment StartX=232.072 StartY=136.221 StartZ=0 EndX=232.072 EndY=-117.815 EndZ=0
    g372: LineSegment StartX=132.072 StartY=136.221 StartZ=0 EndX=132.072 EndY=-121.309 EndZ=0
    g373: LineSegment StartX=245.072 StartY=136.221 StartZ=0 EndX=245.072 EndY=-116.499 EndZ=0
    g374: LineSegment StartX=119.072 StartY=136.221 StartZ=0 EndX=119.072 EndY=-116.228 EndZ=0
    g375: LineSegment StartX=-42.9272 StartY=136.221 StartZ=0 EndX=407.073 EndY=136.221 EndZ=0
    g376: LineSegment StartX=232.072 StartY=136.221 StartZ=0 EndX=220.072 EndY=136.221 EndZ=0
    g377: LineSegment StartX=232.072 StartY=136.221 StartZ=0 EndX=232.072 EndY=124.221 EndZ=0
    g378: LineSegment StartX=220.072 StartY=136.221 StartZ=0 EndX=220.072 EndY=124.221 EndZ=0
    g379: LineSegment StartX=220.072 StartY=136.221 StartZ=0 EndX=226.072 EndY=136.221 EndZ=0
    g380: LineSegment StartX=220.072 StartY=136.221 StartZ=0 EndX=220.072 EndY=130.221 EndZ=0
    g381: LineSegment StartX=220.072 StartY=124.221 StartZ=0 EndX=226.072 EndY=124.221 EndZ=0
    g382: LineSegment StartX=232.072 StartY=124.221 StartZ=0 EndX=232.072 EndY=127.221 EndZ=0
    g383: LineSegment StartX=232.072 StartY=136.221 StartZ=0 EndX=232.072 EndY=133.221 EndZ=0
    g384-g388: Circle x5 (B-spline internal-alignment scaffolding for g389; pole/knot coordinates omitted)
    g389: BSplineCurve PolesCount=5 KnotsCount=3 Degree=3 IsPeriodic=0
    g390: GeomPoint X=232.072 Y=133.221 Z=0
    g391: GeomPoint X=223.072 Y=130.221 Z=0
    g392: GeomPoint X=232.072 Y=127.221 Z=0
  constraints (658):
    c: Vertical(g0)
    c: Vertical(g1)
    c: Block(g1)
    c: Block(g0)
    c: Weight(g4) = 1
    c: Equal(g4,g5)
    c: Equal(g4,g6)
    c: InternalAlignment(g4,g7)
    c: InternalAlignment(g5,g7)
    c: InternalAlignment(g6,g7)
    c: InternalAlignment(g8,g7)
    c: InternalAlignment(g9,g7)
    c: Weight(g10) = 1
    c: Equal(g10,g11)
    c: Equal(g10,g12)
    c: InternalAlignment(g10,g13)
    c: InternalAlignment(g11,g13)
    c: InternalAlignment(g12,g13)
    c: InternalAlignment(g14,g13)
    c: InternalAlignment(g15,g13)
    c: Block(g13)
    c: Block(g7)
    c: Weight(g16) = 1
    c: Equal(g16,g17)
    c: Equal(g16,g18)
    c: InternalAlignment(g16,g19)
    c: InternalAlignment(g17,g19)
    c: InternalAlignment(g18,g19)
    c: InternalAlignment(g20,g19)
    c: InternalAlignment(g21,g19)
    c: Weight(g22) = 1
    c: Equal(g22,g23)
    c: Equal(g22,g24)
    c: InternalAlignment(g22,g25)
    c: InternalAlignment(g23,g25)
    c: InternalAlignment(g24,g25)
    c: InternalAlignment(g26,g25)
    c: InternalAlignment(g27,g25)
    c: Block(g25)
    c: Block(g19)
    c: Weight(g28) = 1
    c: Equal(g28,g29)
    c: Equal(g28,g30)
    c: InternalAlignment(g28,g31)
    c: InternalAlignment(g29,g31)
    c: InternalAlignment(g30,g31)
    c: InternalAlignment(g32,g31)
    c: InternalAlignment(g33,g31)
    c: Weight(g34) = 1
    c: Equal(g34,g35)
    c: Equal(g34,g36)
    c: InternalAlignment(g34,g37)
    c: InternalAlignment(g35,g37)
    c: InternalAlignment(g36,g37)
    c: InternalAlignment(g38,g37)
    c: InternalAlignment(g39,g37)
    c: Block(g31)
    c: Block(g37)
    c: Coincident(g40,g1)
    c: Coincident(g40,g0)
    c: Horizontal(g40)
    c: Distance(g40) = 450
    c: Weight(g41) = 1
    c: Equal(g41,g42)
    c: Equal(g41,g43)
    c: InternalAlignment(g41,g44)
    c: InternalAlignment(g42,g44)
    c: InternalAlignment(g43,g44)
    c: InternalAlignment(g45,g44)
    c: InternalAlignment(g46,g44)
    c: Block(g44)
    c: Weight(g47) = 1
    c: Equal(g47,g48)
    c: Equal(g47,g49)
    c: InternalAlignment(g47,g50)
    c: InternalAlignment(g48,g50)
    c: InternalAlignment(g49,g50)
    c: InternalAlignment(g51,g50)
    c: InternalAlignment(g52,g50)
    c: Block(g50)
    c: Weight(g53) = 1
    c: Equal(g53,g54)
    c: Equal(g53,g55)
    c: InternalAlignment(g53,g56)
    c: InternalAlignment(g54,g56)
    c: InternalAlignment(g55,g56)
    c: InternalAlignment(g57,g56)
    c: InternalAlignment(g58,g56)
    c: Block(g56)
    c: Weight(g59) = 1
    c: Equal(g59,g60)
    c: Equal(g59,g61)
    c: InternalAlignment(g59,g62)
    c: InternalAlignment(g60,g62)
    c: InternalAlignment(g61,g62)
    c: InternalAlignment(g63,g62)
    c: InternalAlignment(g64,g62)
    c: Block(g62)
    c: Weight(g65) = 1
    c: Equal(g65,g66)
    c: Equal(g65,g67)
    c: InternalAlignment(g65,g68)
    c: InternalAlignment(g66,g68)
    c: InternalAlignment(g67,g68)
    c: InternalAlignment(g69,g68)
    c: InternalAlignment(g70,g68)
    c: Weight(g71) = 1
    c: Equal(g71,g72)
    c: Equal(g71,g73)
    c: InternalAlignment(g71,g74)
    c: InternalAlignment(g72,g74)
    c: InternalAlignment(g73,g74)
    c: InternalAlignment(g75,g74)
    c: InternalAlignment(g76,g74)
    c: Block(g68)
    c: Block(g74)
    c: Coincident(g77,g68)
    c: Coincident(g77,g74)
    c: Vertical(g77)
    c: Coincident(g78,g68)
    c: Coincident(g78,g50)
    c: Coincident(g79,g50)
    c: Coincident(g79,g74)
    c: Weight(g80) = 1
    c: Equal(g80,g81)
    c: Equal(g80,g82)
    c: InternalAlignment(g80,g83)
    c: InternalAlignment(g81,g83)
    c: InternalAlignment(g82,g83)
    c: InternalAlignment(g84,g83)
    c: InternalAlignment(g85,g83)
    c: Weight(g86) = 1
    c: Equal(g86,g87)
    c: Equal(g86,g88)
    c: InternalAlignment(g86,g89)
    c: InternalAlignment(g87,g89)
    c: InternalAlignment(g88,g89)
    c: InternalAlignment(g90,g89)
    c: InternalAlignment(g91,g89)
    c: Block(g83)
    c: Block(g89)
    c: Coincident(g92,g83)
    c: Coincident(g92,g89)
    c: Vertical(g92)
    c: Coincident(g93,g83)
    c: Coincident(g93,g44)
    c: Coincident(g94,g44)
    c: Coincident(g94,g89)
    c: Weight(g95) = 1
    c: Equal(g95,g96)
    c: Equal(g95,g97)
    c: InternalAlignment(g95,g98)
    c: InternalAlignment(g96,g98)
    c: InternalAlignment(g97,g98)
    c: InternalAlignment(g99,g98)
    c: InternalAlignment(g100,g98)
    c: Weight(g101) = 1
    c: Equal(g101,g102)
    c: Equal(g101,g103)
    c: InternalAlignment(g101,g104)
    c: InternalAlignment(g102,g104)
    c: InternalAlignment(g103,g104)
    c: InternalAlignment(g105,g104)
    c: InternalAlignment(g106,g104)
    c: Block(g98)
    c: Block(g104)
    c: Coincident(g107,g98)
    c: Coincident(g107,g104)
    c: Vertical(g107)
    c: Coincident(g108,g104)
    c: Coincident(g108,g62)
    c: Coincident(g109,g62)
    c: Coincident(g109,g98)
    c: Weight(g110) = 1
    c: Equal(g110,g111)
    c: Equal(g110,g112)
    c: InternalAlignment(g110,g113)
    c: InternalAlignment(g111,g113)
    c: InternalAlignment(g112,g113)
    c: InternalAlignment(g114,g113)
    c: InternalAlignment(g115,g113)
    c: Weight(g116) = 1
    c: Equal(g116,g117)
    c: Equal(g116,g118)
    c: InternalAlignment(g116,g119)
    c: InternalAlignment(g117,g119)
    c: InternalAlignment(g118,g119)
    c: InternalAlignment(g120,g119)
    c: InternalAlignment(g121,g119)
    c: Block(g113)
    c: Block(g119)
    c: Coincident(g122,g113)
    c: Coincident(g122,g119)
    c: Vertical(g122)
    c: Coincident(g123,g119)
    c: Coincident(g123,g56)
    c: Coincident(g124,g56)
    c: Coincident(g124,g113)
    c: Weight(g125) = 1
    c: Equal(g125,g126)
    c: Equal(g125,g127)
    c: InternalAlignment(g125,g128)
    c: InternalAlignment(g126,g128)
    c: InternalAlignment(g127,g128)
    c: InternalAlignment(g129,g128)
    c: InternalAlignment(g130,g128)
    c: Weight(g131) = 1
    c: Equal(g131,g132)
    c: Equal(g131,g133)
    c: InternalAlignment(g131,g134)
    c: InternalAlignment(g132,g134)
    c: InternalAlignment(g133,g134)
    c: InternalAlignment(g135,g134)
    c: InternalAlignment(g136,g134)
    c: Weight(g137) = 1
    c: Equal(g137,g138)
    c: Equal(g137,g139)
    c: InternalAlignment(g137,g140)
    c: InternalAlignment(g138,g140)
    c: InternalAlignment(g139,g140)
    c: InternalAlignment(g141,g140)
    c: InternalAlignment(g142,g140)
    c: Weight(g143) = 1
    c: Equal(g143,g144)
    c: Equal(g143,g145)
    c: InternalAlignment(g143,g146)
    c: InternalAlignment(g144,g146)
    c: InternalAlignment(g145,g146)
    c: InternalAlignment(g147,g146)
    c: InternalAlignment(g148,g146)
    c: Block(g146)
    c: Block(g140)
    c: Block(g134)
    c: Block(g128)
    c: Coincident(g149,g25)
    c: Coincident(g149,g146)
    c: Coincident(g150,g146)
    c: Coincident(g150,g140)
    c: Horizontal(g150)
    c: Coincident(g151,g140)
    c: Coincident(g151,g25)
    c: Vertical(g151)
    c: Coincident(g152,g19)
    c: Coincident(g152,g134)
    c: Vertical(g152)
    c: Coincident(g153,g134)
    c: Coincident(g153,g128)
    c: Horizontal(g153)
    c: Coincident(g154,g128)
    c: Coincident(g154,g19)
    c: Weight(g155) = 1
    c: Equal(g155,g156)
    c: Equal(g155,g157)
    c: InternalAlignment(g155,g158)
    c: InternalAlignment(g156,g158)
    c: InternalAlignment(g157,g158)
    c: InternalAlignment(g159,g158)
    c: InternalAlignment(g160,g158)
    c: Weight(g161) = 1
    c: Equal(g161,g162)
    c: Equal(g161,g163)
    c: InternalAlignment(g161,g164)
    c: InternalAlignment(g162,g164)
    c: InternalAlignment(g163,g164)
    c: InternalAlignment(g165,g164)
    c: InternalAlignment(g166,g164)
    c: Weight(g167) = 1
    c: Equal(g167,g168)
    c: Equal(g167,g169)
    c: InternalAlignment(g167,g170)
    c: InternalAlignment(g168,g170)
    c: InternalAlignment(g169,g170)
    c: InternalAlignment(g171,g170)
    c: InternalAlignment(g172,g170)
    c: Weight(g173) = 1
    c: Equal(g173,g174)
    c: Equal(g173,g175)
    c: InternalAlignment(g173,g176)
    c: InternalAlignment(g174,g176)
    c: InternalAlignment(g175,g176)
    c: InternalAlignment(g177,g176)
    c: InternalAlignment(g178,g176)
    c: Block(g176)
    c: Block(g170)
    c: Block(g164)
    c: Block(g158)
    c: Coincident(g179,g176)
    c: Coincident(g179,g170)
    c: Horizontal(g179)
    c: Coincident(g180,g170)
    c: Coincident(g180,g7)
    c: Vertical(g180)
    c: Coincident(g181,g13)
    c: Coincident(g181,g164)
    c: Vertical(g181)
    c: Coincident(g182,g158)
    c: Coincident(g182,g13)
    c: Coincident(g183,g7)
    c: Weight(g184) = 1
    c: Equal(g184,g185)
    c: Equal(g184,g186)
    c: InternalAlignment(g184,g187)
    c: InternalAlignment(g185,g187)
    c: InternalAlignment(g186,g187)
    c: InternalAlignment(g188,g187)
    c: InternalAlignment(g189,g187)
    c: Weight(g190) = 1
    c: Equal(g190,g191)
    c: Equal(g190,g192)
    c: InternalAlignment(g190,g193)
    c: InternalAlignment(g191,g193)
    c: InternalAlignment(g192,g193)
    c: InternalAlignment(g194,g193)
    c: InternalAlignment(g195,g193)
    c: Block(g193)
    c: Block(g187)
    c: Coincident(g196,g193)
    c: Coincident(g196,g31)
    c: Coincident(g197,g31)
    c: Coincident(g197,g187)
    c: Coincident(g198,g187)
    c: Coincident(g198,g193)
    c: Vertical(g198)
    c: Weight(g199) = 1
    c: Equal(g199,g200)
    c: Equal(g199,g201)
    c: InternalAlignment(g199,g202)
    c: InternalAlignment(g200,g202)
    c: InternalAlignment(g201,g202)
    c: InternalAlignment(g203,g202)
    c: InternalAlignment(g204,g202)
    c: Weight(g205) = 1
    c: Equal(g205,g206)
    c: Equal(g205,g207)
    c: InternalAlignment(g205,g208)
    c: InternalAlignment(g206,g208)
    c: InternalAlignment(g207,g208)
    c: InternalAlignment(g209,g208)
    c: InternalAlignment(g210,g208)
    c: Block(g208)
    c: Block(g202)
    c: Coincident(g211,g202)
    c: Coincident(g211,g37)
    c: Coincident(g212,g37)
    c: Coincident(g212,g208)
    c: Coincident(g213,g208)
    c: Coincident(g213,g202)
    c: Vertical(g213)
    c: Horizontal(g214)
    c: Block(g214)
    c: Vertical(g215)
    c: Block(g215)
    c: Block(g216)
    c: Weight(g217) = 1
    c: Equal(g217,g218)
    c: Equal(g217,g219)
    c: InternalAlignment(g217,g220)
    c: InternalAlignment(g218,g220)
    c: InternalAlignment(g219,g220)
    c: InternalAlignment(g221,g220)
    c: InternalAlignment(g222,g220)
    c: Weight(g223) = 1
    c: Equal(g223,g224)
    c: Equal(g223,g225)
    c: InternalAlignment(g223,g226)
    c: InternalAlignment(g224,g226)
    c: InternalAlignment(g225,g226)
    c: InternalAlignment(g227,g226)
    c: InternalAlignment(g228,g226)
    c: Weight(g229) = 1
    c: Equal(g229,g230)
    c: Equal(g229,g231)
    c: InternalAlignment(g229,g232)
    c: InternalAlignment(g230,g232)
    c: InternalAlignment(g231,g232)
    c: InternalAlignment(g233,g232)
    c: InternalAlignment(g234,g232)
    c: Weight(g235) = 1
    c: Equal(g235,g236)
    c: Equal(g235,g237)
    c: InternalAlignment(g235,g238)
    c: InternalAlignment(g236,g238)
    c: InternalAlignment(g237,g238)
    c: InternalAlignment(g239,g238)
    c: InternalAlignment(g240,g238)
    c: Block(g220)
    c: Block(g226)
    c: Block(g232)
    c: Block(g238)
    c: Coincident(g241,g226)
    c: Coincident(g241,g220)
    c: Horizontal(g241)
    c: Block(g183)
    c: Weight(g242) = 1
    c: Equal(g242,g243)
    c: Equal(g242,g244)
    c: InternalAlignment(g242,g245)
    c: InternalAlignment(g243,g245)
    c: InternalAlignment(g244,g245)
    c: InternalAlignment(g246,g245)
    c: InternalAlignment(g247,g245)
    c: Weight(g248) = 1
    c: Equal(g248,g249)
    c: Equal(g248,g250)
    c: InternalAlignment(g248,g251)
    c: InternalAlignment(g249,g251)
    c: InternalAlignment(g250,g251)
    c: InternalAlignment(g252,g251)
    c: InternalAlignment(g253,g251)
    c: Block(g245)
    c: Block(g251)
    c: Coincident(g254,g245)
    c: Coincident(g254,g251)
    c: Weight(g255) = 1
    c: Equal(g255,g256)
    c: Equal(g255,g257)
    c: InternalAlignment(g255,g258)
    c: InternalAlignment(g256,g258)
    c: InternalAlignment(g257,g258)
    c: InternalAlignment(g259,g258)
    c: InternalAlignment(g260,g258)
    c: Weight(g261) = 1
    c: Equal(g261,g262)
    c: Equal(g261,g263)
    c: InternalAlignment(g261,g264)
    c: InternalAlignment(g262,g264)
    c: InternalAlignment(g263,g264)
    c: InternalAlignment(g265,g264)
    c: InternalAlignment(g266,g264)
    c: Weight(g267) = 1
    c: Equal(g267,g268)
    c: Equal(g267,g269)
    c: InternalAlignment(g267,g270)
    c: InternalAlignment(g268,g270)
    c: InternalAlignment(g269,g270)
    c: InternalAlignment(g271,g270)
    c: InternalAlignment(g272,g270)
    c: Block(g270)
    c: Block(g264)
    c: Block(g258)
    c: Coincident(g273,g264)
    c: Coincident(g273,g258)
    c: Coincident(g274,g258)
    c: Coincident(g274,g270)
    c: Vertical(g274)
    c: Coincident(g275,g270)
    c: Coincident(g275,g264)
    c: Horizontal(g275)
    c: Weight(g276) = 1
    c: Equal(g276,g277)
    c: InternalAlignment(g276,g278)
    c: InternalAlignment(g277,g278)
    c: InternalAlignment(g279,g278)
    c: InternalAlignment(g280,g278)
    c: Weight(g281) = 1
    c: InternalAlignment(g282,g284)
    c: InternalAlignment(g283,g284)
    c: InternalAlignment(g285,g284)
    c: InternalAlignment(g286,g284)
    c: Weight(g287) = 1
    c: Equal(g287,g288)
    c: Equal(g287,g289)
    c: InternalAlignment(g287,g290)
    c: InternalAlignment(g288,g290)
    c: InternalAlignment(g289,g290)
    c: InternalAlignment(g291,g290)
    c: InternalAlignment(g292,g290)
    c: Equal(g293,g294)
    c: Equal(g293,g295)
    c: InternalAlignment(g293,g296)
    c: InternalAlignment(g294,g296)
    c: InternalAlignment(g295,g296)
    c: InternalAlignment(g297,g296)
    c: InternalAlignment(g298,g296)
    c: Block(g284)
    c: Block(g290)
    c: Block(g296)
    c: Block(g278)
    c: Coincident(g299,g278)
    c: Coincident(g299,g284)
    c: Horizontal(g299)
    c: Coincident(g300,g284)
    c: Coincident(g300,g290)
    c: Vertical(g300)
    c: Coincident(g301,g290)
    c: Coincident(g301,g296)
    c: Horizontal(g301)
    c: Coincident(g302,g296)
    c: Coincident(g302,g278)
    c: Weight(g303) = 1
    c: Equal(g303,g304)
    c: Equal(g303,g305)
    c: InternalAlignment(g303,g306)
    c: InternalAlignment(g304,g306)
    c: InternalAlignment(g305,g306)
    c: InternalAlignment(g307,g306)
    c: InternalAlignment(g308,g306)
    c: Weight(g309) = 1
    c: Equal(g309,g310)
    c: Equal(g309,g311)
    c: InternalAlignment(g309,g312)
    c: InternalAlignment(g310,g312)
    c: InternalAlignment(g311,g312)
    c: InternalAlignment(g313,g312)
    c: InternalAlignment(g314,g312)
    c: Weight(g315) = 1
    c: Equal(g315,g316)
    c: Equal(g315,g317)
    c: InternalAlignment(g315,g318)
    c: InternalAlignment(g316,g318)
    c: InternalAlignment(g317,g318)
    c: InternalAlignment(g319,g318)
    c: InternalAlignment(g320,g318)
    c: Block(g318)
    c: Block(g312)
    c: Block(g306)
    c: Coincident(g321,g318)
    c: Coincident(g321,g312)
    c: Horizontal(g321)
    c: Coincident(g322,g312)
    c: Coincident(g322,g306)
    c: Vertical(g322)
    c: Coincident(g323,g306)
    c: Coincident(g323,g318)
    c: InternalAlignment(g324,g325)
    c: InternalAlignment(g326,g325)
    c: InternalAlignment(g327,g325)
    c: Block(g325)
    c: Equal(g328,g329)
    c: Equal(g328,g330)
    c: InternalAlignment(g328,g331)
    c: InternalAlignment(g329,g331)
    c: InternalAlignment(g330,g331)
    c: InternalAlignment(g332,g331)
    c: InternalAlignment(g333,g331)
    c: Block(g331)
    c: Coincident(g334,g325)
    c: Horizontal(g334)
    c: Block(g334)
    c: Coincident(g335,g325)
    c: Coincident(g335,g251)
    c: Vertical(g335)
    c: Coincident(g336,g331)
    c: Coincident(g336,g245)
    c: Vertical(g336)
    c: Block(g337)
    c: Block(g2)
    c: Distance(g335) = 119.89
    c: Coincident(g338,g337)
    c: Coincident(g338,g2)
    c: Coincident(g339,g2)
    c: Coincident(g339,g337)
    c: Block(g3)
    c: Block(g340)
    c: Coincident(g341,g340)
    c: Coincident(g341,g3)
    c: Coincident(g342,g340)
    c: Coincident(g342,g3)
    c: Block(g342)
    c: Block(g341)
    c: Weight(g343) = 1
    c: Equal(g343,g344)
    c: Equal(g343,g345)
    c: InternalAlignment(g343,g346)
    c: InternalAlignment(g344,g346)
    c: InternalAlignment(g345,g346)
    c: InternalAlignment(g347,g346)
    c: InternalAlignment(g348,g346)
    c: Weight(g349) = 1
    c: Equal(g349,g350)
    c: Equal(g349,g351)
    c: InternalAlignment(g349,g352)
    c: InternalAlignment(g350,g352)
    c: InternalAlignment(g351,g352)
    c: InternalAlignment(g353,g352)
    c: InternalAlignment(g354,g352)
    c: Weight(g355) = 1
    c: Equal(g355,g356)
    c: Equal(g355,g357)
    c: InternalAlignment(g355,g358)
    c: InternalAlignment(g356,g358)
    c: InternalAlignment(g357,g358)
    c: InternalAlignment(g359,g358)
    c: InternalAlignment(g360,g358)
    c: Weight(g361) = 1
    c: Equal(g361,g362)
    c: Equal(g361,g363)
    c: InternalAlignment(g361,g364)
    c: InternalAlignment(g362,g364)
    c: InternalAlignment(g363,g364)
    c: InternalAlignment(g365,g364)
    c: InternalAlignment(g366,g364)
    c: Block(g364)
    c: Block(g358)
    c: Block(g352)
    c: Block(g346)
    c: Coincident(g367,g364)
    c: Coincident(g367,g346)
    c: Vertical(g367)
    c: Coincident(g368,g346)
    c: Coincident(g368,g352)
    c: Coincident(g369,g352)
    c: Coincident(g369,g358)
    c: Vertical(g369)
    c: Coincident(g370,g358)
    c: Coincident(g370,g364)
    c: Horizontal(g370)
    c: Vertical(g371)
    c: Vertical(g372)
    c: Vertical(g373)
    c: Vertical(g374)
    c: Coincident(g375,g0)
    c: Coincident(g375,g1)
    c: Horizontal(g375)
    c: Block(g375)
    c: Distance(g375) = 450
    c: Block(g373)
    c: Block(g371)
    c: Block(g372)
    c: Block(g374)
    c: Distance(g0) = 240
    c: Horizontal(g376)
    c: Distance(g376) = 12
    c: Coincident(g376,g371)
    c: Vertical(g377)
    c: Distance(g377) = 12
    c: Coincident(g377,g371)
    c: Coincident(g378,g376)
    c: Vertical(g378)
    c: Horizontal(g379)
    c: Vertical(g380)
    c: Distance(g380) = 6
    c: Coincident(g380,g376)
    c: Coincident(g379,g376)
    c: Block(g378)
    c: Coincident(g381,g378)
    c: Horizontal(g381)
    c: Distance(g381) = 6
    c: Vertical(g382)
    c: Distance(g382) = 3
    c: Vertical(g383)
    c: Distance(g383) = 3
    c: Coincident(g383,g371)
    c: Coincident(g377,g382)
    c: Coincident(g389,g383)
    c: Weight(g384) = 1
    c: Equal(g384,g385)
    c: Coincident(g385,g379)
    c: Equal(g384,g386)
    c: Coincident(g386,g380)
    c: Equal(g384,g387)
    c: Coincident(g387,g381)
    c: Equal(g384,g388)
    c: Coincident(g389,g382)
    c: InternalAlignment(g384-g388 -> g389) x5
    c: InternalAlignment(g390,g389)
    c: InternalAlignment(g391,g389)
    c: InternalAlignment(g392,g389)
FEATURE [Part::Extrusion] Extrude005
  Base = -> Sketch003
  Dir = (0,0,1)
  DirMode = 2
  FaceMakerClass = Part::FaceMakerBullseye
  LengthFwd = 24
  LengthRev = 0
  Solid = true
  Symmetric = false
